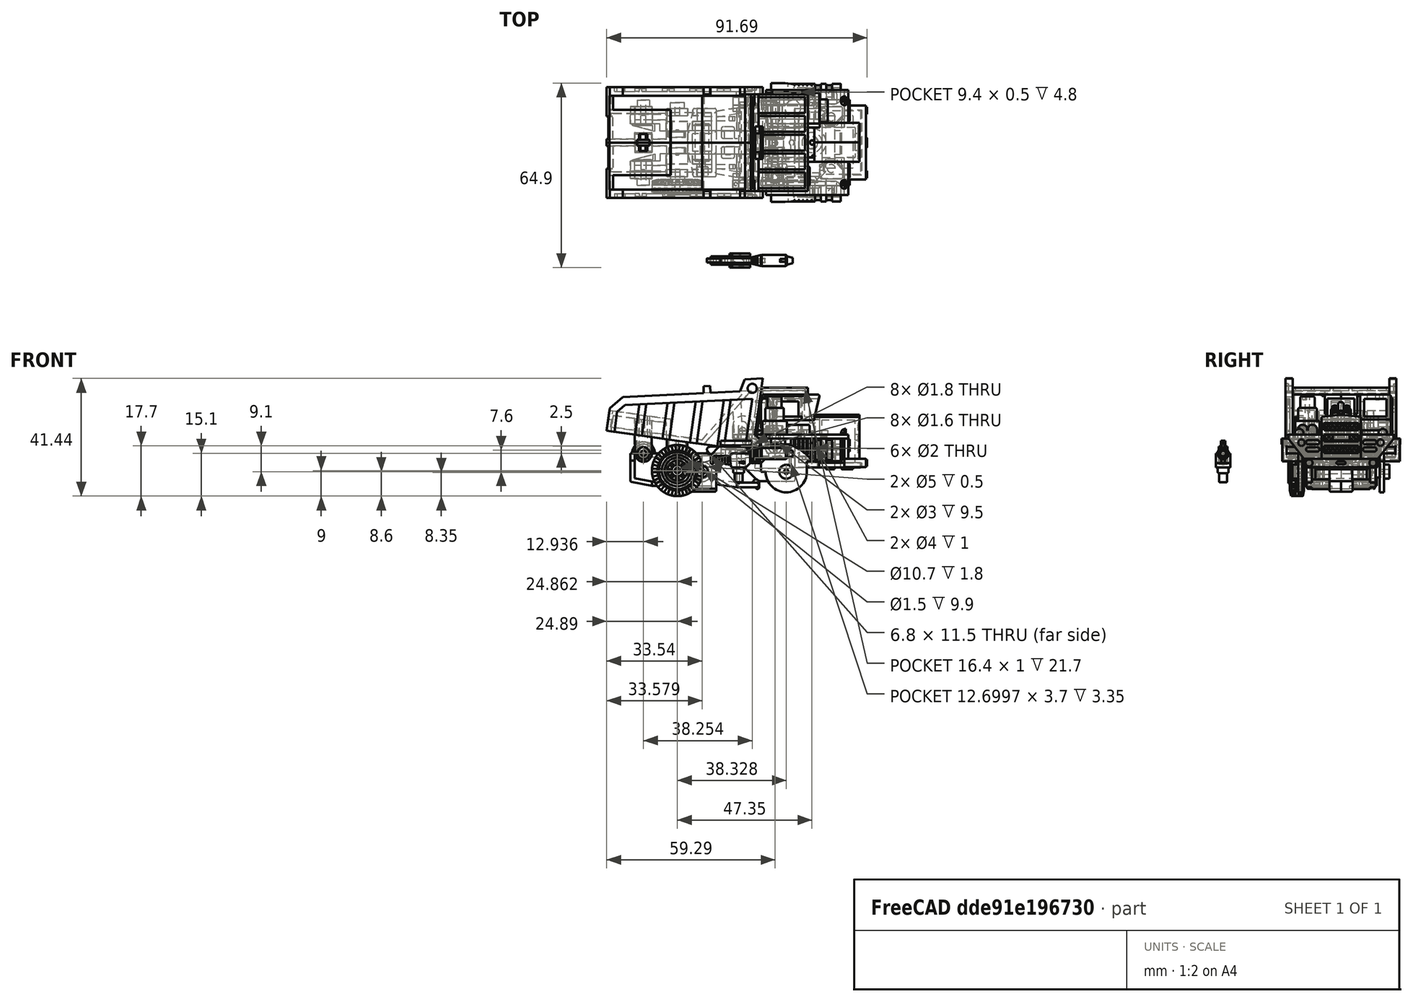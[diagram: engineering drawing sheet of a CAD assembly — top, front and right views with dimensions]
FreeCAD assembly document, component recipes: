
FREECAD ASSEMBLY — COMPONENT RECIPES ("Longhaul")

This assembly document has 21 components, labeled P0..P20 below (a component is one placed body or linked part). 19 of them carry a construction recipe — the FreeCAD feature program that regenerates the part from scratch, quoted from this document or its linked companion documents; the rest are supplied as boundary geometry only. No exploded tour is included for this assembly.
NOTE — document 3 of 4 of this assembly tour. The two overview renders and the header above are repeated from document 1; the component sections below continue where the previous document stopped.
COMPONENT P7 — recipe-attached ("Roof", modeled in this document).
Construction recipe (the document's own serialized feature program — sketch geometry with constraints, then the solid features built on it; lengths are millimeters unless a unit is written):

FEATURE [Sketcher::SketchObject] Sketch335
  ArcFitTolerance = 1e-06
  AttachmentSupport = -> [XY_Plane017]
  FullyConstrained = true
  MakeInternals = false
  MapMode = 5
  sketch-geometry (10):
    g0: LineSegment StartX=0 StartY=0 StartZ=0 EndX=16 EndY=0 EndZ=0
    g1: LineSegment StartX=16 StartY=0 StartZ=0 EndX=16 EndY=1.5 EndZ=0
    g2: LineSegment StartX=16 StartY=1.5 StartZ=0 EndX=-1.4 EndY=1.5 EndZ=0
    g3: LineSegment StartX=0 StartY=0 StartZ=0 EndX=-1.82086 EndY=-12.9561 EndZ=0
    g4: LineSegment StartX=-2.81113 StartY=-13.8169 StartZ=0 EndX=-5.72779 EndY=-13.8169 EndZ=0
    g5: ArcOfCircle CenterX=-6.8767 CenterY=-13.0169 CenterZ=0 NormalX=0 NormalY=0 NormalZ=1 AngleXU=0 Radius=1.4 StartAngle=0.608246 EndAngle=5.67494
    g6: LineSegment StartX=-5.72779 StartY=-12.2169 StartZ=0 EndX=-3.32779 EndY=-12.2169 EndZ=0
    g7: LineSegment StartX=-3.32779 StartY=-12.2169 StartZ=0 EndX=-1.4 EndY=1.5 EndZ=0
    g8: ArcOfCircle CenterX=-2.81113 CenterY=-12.8169 CenterZ=0 NormalX=0 NormalY=0 NormalZ=1 AngleXU=0 Radius=1 StartAngle=4.71239 EndAngle=6.14356
    g9: GeomPoint [constr] X=-1.94184 Y=-13.8169 Z=0
  constraints (28):
    c: Coincident(g0,g-1)
    c: PointOnObject(g0,g-1)
    c: Coincident(g1,g0)
    c: Vertical(g1)
    c: Coincident(g2,g1)
    c: Horizontal(g2)
    c: Coincident(g3,g0)
    c: Horizontal(g4)
    c: Coincident(g5,g4)
    c: Coincident(g6,g5)
    c: Horizontal(g6)
    c: Coincident(g7,g6)
    c: Coincident(g7,g2)
    c: PointOnObject(g9,g3)
    c: PointOnObject(g9,g4)
    c: Tangent(g3,g8) = 1.5708
    c: Tangent(g4,g8) = 1.5708
    c: Parallel(g3,g7)
    c: DistanceY(g4,g5) = 1.6
    c: DistanceY(g1,g1) = 1.5
    c: Distance(g4,g0) = 14.1
    c: DistanceX(g5,g4) = 0
    c: Radius(g8) = 1
    c: DistanceX(g2,g2) = 17.4
    c: Diameter(g5) = 2.8
    c: Angle(g3,g0) = 1.71042
    c: DistanceX(g6,g6) = 2.4
    c: DistanceX(g2,g0) = 1.4
FEATURE [PartDesign::Pad] Pad198
  Direction = (0,0,1)
  Length = 34
  Length2 = 10
  Profile = -> Sketch335
  ReferenceAxis = -> Sketch335 [N_Axis]
  Refine = true
  Suppressed = false
  Type = 0
FEATURE [Sketcher::SketchObject] Sketch336
  ArcFitTolerance = 1e-06
  AttachmentSupport = -> [Pad198]
  ExternalGeometry = -> [Pad198]
  FullyConstrained = true
  MakeInternals = false
  MapMode = 5
  Placement = pos=(0,0,0) rot=(1,0,0;3.14159rad)
  sketch-geometry (2):
    g0: LineSegment StartX=-5.72779 StartY=13.8169 StartZ=0 EndX=-8.02561 EndY=13.8169 EndZ=0
    g1: ArcOfCircle CenterX=-6.8767 CenterY=13.0169 CenterZ=0 NormalX=0 NormalY=0 NormalZ=1 AngleXU=0 Radius=1.39999 StartAngle=0.608239 EndAngle=2.53335
  constraints (6):
    c: Coincident(g0,g-4)
    c: PointOnObject(g0,g-4)
    c: Horizontal(g0)
    c: Coincident(g1,g0)
    c: Coincident(g1,g0)
    c: Tangent(g1,g-4)
FEATURE [PartDesign::Pocket] Pocket141
  BaseFeature = -> Pad198
  Direction = (0,0,1)
  Length = 34
  Length2 = 5
  Profile = -> Sketch336
  ReferenceAxis = -> Sketch336 [N_Axis]
  Refine = true
  Suppressed = false
  Type = 0
FEATURE [Sketcher::SketchObject] Sketch337
  ArcFitTolerance = 1e-06
  AttachmentSupport = -> [Pocket141]
  ExternalGeometry = -> [Pocket141]
  FullyConstrained = true
  MakeInternals = false
  MapMode = 5
  Placement = pos=(0,0,0) rot=(1,0,0;3.14159rad)
  sketch-geometry (7):
    g0: ArcOfCircle CenterX=-2.81113 CenterY=12.8169 CenterZ=0 NormalX=0 NormalY=0 NormalZ=1 AngleXU=0 Radius=1 StartAngle=0.139626 EndAngle=1.5708
    g1: LineSegment StartX=-1.82086 StartY=12.9561 StartZ=0 EndX=-1.125 EndY=8.00476 EndZ=0
    g2: LineSegment StartX=-1.125 StartY=8.00476 StartZ=0 EndX=-2.73581 EndY=8.00476 EndZ=0
    g3: LineSegment StartX=-2.81113 StartY=13.8169 StartZ=0 EndX=-8.02561 EndY=13.8169 EndZ=0
    g4: ArcOfCircle CenterX=-6.8767 CenterY=13.0169 CenterZ=0 NormalX=0 NormalY=0 NormalZ=1 AngleXU=0 Radius=1.4 StartAngle=2.53335 EndAngle=5.67494
    g5: LineSegment StartX=-5.72779 StartY=12.2169 StartZ=0 EndX=-3.32779 EndY=12.2169 EndZ=0
    g6: LineSegment StartX=-3.32779 StartY=12.2169 StartZ=0 EndX=-2.73581 EndY=8.00476 EndZ=0
  constraints (17):
    c: Tangent(g0,g-4) = -1.5708
    c: Coincident(g0,g-5)
    c: Radius(g0) = 1
    c: Coincident(g1,g0)
    c: PointOnObject(g1,g-5)
    c: Distance(g1) = 5
    c: Coincident(g2,g1)
    c: PointOnObject(g2,g-6)
    c: Horizontal(g2)
    c: Coincident(g3,g0)
    c: Coincident(g3,g-8)
    c: Coincident(g4,g3)
    c: Tangent(g4,g-8) = -1.5708
    c: Coincident(g5,g4)
    c: Coincident(g5,g-7)
    c: Coincident(g6,g5)
    c: Coincident(g6,g2)
FEATURE [PartDesign::Pocket] Pocket142
  BaseFeature = -> Pocket141
  Direction = (0,0,1)
  Length = 2.6
  Length2 = 5
  Profile = -> Sketch337
  ReferenceAxis = -> Sketch337 [N_Axis]
  Refine = true
  Suppressed = false
  Type = 0
FEATURE [Sketcher::SketchObject] Sketch338
  ArcFitTolerance = 1e-06
  AttachmentSupport = -> [Pocket142]
  ExternalGeometry = -> [Pocket142]
  FullyConstrained = true
  MakeInternals = false
  MapMode = 5
  Placement = pos=(0,0,34) rot=(0,0,1;0rad)
  sketch-geometry (7):
    g0: ArcOfCircle CenterX=-2.81113 CenterY=-12.8169 CenterZ=0 NormalX=0 NormalY=0 NormalZ=1 AngleXU=0 Radius=1 StartAngle=4.71239 EndAngle=6.14356
    g1: LineSegment StartX=-1.82086 StartY=-12.9561 StartZ=0 EndX=-1.125 EndY=-8.00476 EndZ=0
    g2: LineSegment StartX=-2.81113 StartY=-13.8169 StartZ=0 EndX=-8.02561 EndY=-13.8169 EndZ=0
    g3: ArcOfCircle CenterX=-6.8767 CenterY=-13.0169 CenterZ=0 NormalX=0 NormalY=0 NormalZ=1 AngleXU=0 Radius=1.4 StartAngle=0.608251 EndAngle=3.74983
    g4: LineSegment StartX=-5.72779 StartY=-12.2169 StartZ=0 EndX=-3.32779 EndY=-12.2169 EndZ=0
    g5: LineSegment StartX=-1.125 StartY=-8.00476 StartZ=0 EndX=-2.73581 EndY=-8.00476 EndZ=0
    g6: LineSegment StartX=-2.73581 StartY=-8.00476 StartZ=0 EndX=-3.32779 EndY=-12.2169 EndZ=0
  constraints (17):
    c: Coincident(g0,g-5)
    c: Tangent(g0,g-4) = -1.5708
    c: Coincident(g1,g0)
    c: PointOnObject(g1,g-3)
    c: Distance(g1) = 5
    c: Coincident(g2,g0)
    c: Coincident(g2,g-6)
    c: Coincident(g3,g2)
    c: Coincident(g3,g-7)
    c: Tangent(g3,g-6)
    c: Coincident(g4,g3)
    c: Coincident(g4,g-8)
    c: Coincident(g5,g1)
    c: PointOnObject(g5,g-8)
    c: Horizontal(g5)
    c: Coincident(g6,g5)
    c: Coincident(g6,g4)
FEATURE [PartDesign::Pocket] Pocket143
  BaseFeature = -> Pocket142
  Direction = (0,0,-1)
  Length = 2.6
  Length2 = 5
  Profile = -> Sketch338
  ReferenceAxis = -> Sketch338 [N_Axis]
  Refine = true
  Suppressed = false
  Type = 0
FEATURE [Sketcher::SketchObject] Sketch339
  ArcFitTolerance = 1e-06
  AttachmentSupport = -> [Pocket143]
  ExternalGeometry = -> [Pocket143]
  FullyConstrained = true
  MakeInternals = false
  MapMode = 5
  Placement = pos=(0,0,31.4) rot=(0,0,1;0rad)
  sketch-geometry (7):
    g0: ArcOfCircle CenterX=-6.8767 CenterY=-13.0169 CenterZ=0 NormalX=0 NormalY=0 NormalZ=1 AngleXU=0 Radius=1.4 StartAngle=5.67495 EndAngle=6.89144
    g1: LineSegment StartX=-5.72778 StartY=-13.8169 StartZ=0 EndX=-2.81113 EndY=-13.8169 EndZ=0
    g2: LineSegment StartX=-5.72779 StartY=-12.2169 StartZ=0 EndX=-3.32779 EndY=-12.2169 EndZ=0
    g3: LineSegment StartX=-3.32779 StartY=-12.2169 StartZ=0 EndX=-2.73581 EndY=-8.00476 EndZ=0
    g4: LineSegment StartX=-2.73581 StartY=-8.00476 StartZ=0 EndX=-1.125 EndY=-8.00476 EndZ=0
    g5: ArcOfCircle CenterX=-2.81113 CenterY=-12.8169 CenterZ=0 NormalX=0 NormalY=0 NormalZ=1 AngleXU=0 Radius=1 StartAngle=4.71239 EndAngle=6.14356
    g6: LineSegment StartX=-1.125 StartY=-8.00476 StartZ=0 EndX=-1.82086 EndY=-12.9561 EndZ=0
  constraints (15):
    c: PointOnObject(g0,g-8)
    c: Coincident(g0,g-7)
    c: Coincident(g1,g0)
    c: Coincident(g1,g-9)
    c: Coincident(g0,g-7)
    c: Coincident(g2,g0)
    c: Coincident(g2,g-6)
    c: Coincident(g3,g2)
    c: Coincident(g3,g-5)
    c: Coincident(g4,g3)
    c: Coincident(g4,g-4)
    c: Coincident(g5,g1)
    c: Tangent(g5,g-9) = -1.5708
    c: Coincident(g6,g4)
    c: Coincident(g6,g5)
FEATURE [PartDesign::Pocket] Pocket144
  BaseFeature = -> Pocket143
  Direction = (0,0,-1)
  Length = 1.3
  Length2 = 5
  Profile = -> Sketch339
  ReferenceAxis = -> Sketch339 [N_Axis]
  Refine = true
  Suppressed = false
  Type = 0
FEATURE [Sketcher::SketchObject] Sketch340
  ArcFitTolerance = 1e-06
  AttachmentSupport = -> [Pocket144]
  ExternalGeometry = -> [Pocket144]
  FullyConstrained = true
  MakeInternals = false
  MapMode = 5
  Placement = pos=(0,0,2.6) rot=(1,0,0;3.14159rad)
  sketch-geometry (7):
    g0: ArcOfCircle CenterX=-6.8767 CenterY=13.0169 CenterZ=0 NormalX=0 NormalY=0 NormalZ=1 AngleXU=0 Radius=1.4 StartAngle=5.67494 EndAngle=6.89143
    g1: ArcOfCircle CenterX=-2.81113 CenterY=12.8169 CenterZ=0 NormalX=0 NormalY=0 NormalZ=1 AngleXU=0 Radius=1 StartAngle=0.139626 EndAngle=1.5708
    g2: LineSegment StartX=-5.72779 StartY=13.8169 StartZ=0 EndX=-2.81113 EndY=13.8169 EndZ=0
    g3: LineSegment StartX=-5.72779 StartY=12.2169 StartZ=0 EndX=-3.32779 EndY=12.2169 EndZ=0
    g4: LineSegment StartX=-1.82086 StartY=12.9561 StartZ=0 EndX=-1.125 EndY=8.00476 EndZ=0
    g5: LineSegment StartX=-3.32779 StartY=12.2169 StartZ=0 EndX=-2.73581 EndY=8.00476 EndZ=0
    g6: LineSegment StartX=-2.73581 StartY=8.00476 StartZ=0 EndX=-1.125 EndY=8.00476 EndZ=0
  constraints (15):
    c: Coincident(g0,g-7)
    c: PointOnObject(g0,g-5)
    c: Coincident(g0,g-7)
    c: Coincident(g1,g-5)
    c: Tangent(g1,g-4) = -1.5708
    c: Coincident(g2,g0)
    c: Coincident(g2,g1)
    c: Coincident(g3,g0)
    c: Coincident(g3,g-6)
    c: Coincident(g4,g1)
    c: Coincident(g4,g-8)
    c: Coincident(g5,g3)
    c: Coincident(g5,g-8)
    c: Coincident(g6,g5)
    c: Coincident(g6,g4)
FEATURE [PartDesign::Pocket] Pocket145
  BaseFeature = -> Pocket144
  Direction = (0,0,1)
  Length = 1.3
  Length2 = 5
  Profile = -> Sketch340
  ReferenceAxis = -> Sketch340 [N_Axis]
  Refine = true
  Suppressed = false
  Type = 0
FEATURE [Sketcher::SketchObject] Sketch341
  ArcFitTolerance = 1e-06
  AttachmentSupport = -> [Pocket145]
  ExternalGeometry = -> [Pocket145]
  FullyConstrained = true
  MakeInternals = false
  MapMode = 5
  Placement = pos=(-1.57961,0.222,0) rot=(-0.523661,0.602403,0.602403;4.10639rad)
  sketch-geometry (4):
    g0: LineSegment StartX=12.5612 StartY=13.75 StartZ=0 EndX=12.5612 EndY=20.25 EndZ=0
    g1: LineSegment StartX=12.5612 StartY=20.25 StartZ=0 EndX=11.5612 EndY=20.25 EndZ=0
    g2: LineSegment StartX=11.5612 StartY=20.25 StartZ=0 EndX=11.5612 EndY=13.75 EndZ=0
    g3: LineSegment StartX=11.5612 StartY=13.75 StartZ=0 EndX=12.5612 EndY=13.75 EndZ=0
  constraints (14):
    c: Coincident(g0,g1)
    c: Coincident(g1,g2)
    c: Coincident(g2,g3)
    c: Coincident(g3,g0)
    c: Vertical(g0)
    c: Vertical(g2)
    c: Horizontal(g1)
    c: Horizontal(g3)
    c: PointOnObject(g0,g-4)
    c: DistanceY(g2,g2) = 6.5
    c: DistanceX(g3,g3) = 1
    c: DistanceY(g-4,g-5) = 26.2
    c: DistanceY(g-3,g-3) = 0
    c: DistanceY(g-4,g0) = 9.85
FEATURE [PartDesign::Pad] Pad199
  BaseFeature = -> Pocket145
  Direction = (-0.990268,0.139173,0)
  Length = 0.5
  Length2 = 10
  Profile = -> Sketch341
  ReferenceAxis = -> Sketch341 [N_Axis]
  Refine = true
  Suppressed = false
  Type = 0
FEATURE [Sketcher::SketchObject] Sketch342
  ArcFitTolerance = 1e-06
  AttachmentSupport = -> [Pad199]
  ExternalGeometry = -> [Pad199]
  FullyConstrained = false
  MakeInternals = false
  MapMode = 5
  Placement = pos=(-2.07475,0.291586,0) rot=(-0.523661,0.602403,0.602403;4.10639rad)
  sketch-geometry (4):
    g0: LineSegment StartX=12.5612 StartY=20.25 StartZ=0 EndX=12.5612 EndY=13.75 EndZ=0
    g1: LineSegment StartX=12.5612 StartY=13.75 StartZ=0 EndX=13.9707 EndY=13.75 EndZ=0
    g2: LineSegment StartX=13.9707 StartY=13.75 StartZ=0 EndX=13.9707 EndY=20.25 EndZ=0
    g3: LineSegment StartX=13.9707 StartY=20.25 StartZ=0 EndX=12.5612 EndY=20.25 EndZ=0
  constraints (9):
    c: Coincident(g0,g1)
    c: Coincident(g1,g2)
    c: Coincident(g2,g3)
    c: Coincident(g3,g0)
    c: Vertical(g2)
    c: Horizontal(g1)
    c: Horizontal(g3)
    c: Coincident(g0,g-5)
    c: Coincident(g0,g-5)
FEATURE [PartDesign::Pad] Pad200
  BaseFeature = -> Pad199
  Direction = (-0.990268,0.139173,2e-16)
  Length = 0.5
  Length2 = 10
  Profile = -> Sketch342
  ReferenceAxis = -> Sketch342 [N_Axis]
  Refine = true
  Reversed = true
  Suppressed = false
  Type = 0
FEATURE [Sketcher::SketchObject] Sketch343
  ArcFitTolerance = 1e-06
  AttachmentSupport = -> [Pad200]
  ExternalGeometry = -> [Pad200]
  FullyConstrained = true
  MakeInternals = false
  MapMode = 5
  Placement = pos=(-1.57961,0.222,0) rot=(-0.523661,0.602403,0.602403;4.10639rad)
  sketch-geometry (4):
    g0: LineSegment StartX=-1.29056 StartY=22.7 StartZ=0 EndX=-1.29056 EndY=11.3 EndZ=0
    g1: LineSegment StartX=-1.29056 StartY=11.3 StartZ=0 EndX=5.90944 EndY=11.3 EndZ=0
    g2: LineSegment StartX=5.90944 StartY=11.3 StartZ=0 EndX=5.90944 EndY=22.7 EndZ=0
    g3: LineSegment StartX=5.90944 StartY=22.7 StartZ=0 EndX=-1.29056 EndY=22.7 EndZ=0
  constraints (13):
    c: Coincident(g0,g1)
    c: Coincident(g1,g2)
    c: Coincident(g2,g3)
    c: Coincident(g3,g0)
    c: Vertical(g0)
    c: Vertical(g2)
    c: Horizontal(g1)
    c: Horizontal(g3)
    c: PointOnObject(g0,g-3)
    c: DistanceY(g2,g2) = 11.4
    c: DistanceX(g3,g3) = 7.2
    c: DistanceY(g-3,g-3) = 34
    c: DistanceY(g-3,g0) = 11.3
FEATURE [PartDesign::Pocket] Pocket146
  BaseFeature = -> Pad200
  Direction = (0.990268,-0.139173,0)
  Length = 1.6
  Length2 = 5
  Profile = -> Sketch343
  ReferenceAxis = -> Sketch343 [N_Axis]
  Refine = true
  Suppressed = false
  Type = 0
FEATURE [Sketcher::SketchObject] Sketch344
  ArcFitTolerance = 1e-06
  AttachmentSupport = -> [Pocket146]
  ExternalGeometry = -> [Pocket146]
  FullyConstrained = true
  MakeInternals = false
  MapMode = 5
  Placement = pos=(0,1.5,0) rot=(0,0.707107,0.707107;3.14159rad)
  sketch-geometry (24):
    g0: LineSegment StartX=1.4 StartY=0 StartZ=0 EndX=1.4 EndY=1 EndZ=0
    g1: LineSegment StartX=1.4 StartY=1 StartZ=0 EndX=-15 EndY=1 EndZ=0
    g2: LineSegment StartX=-15 StartY=1 StartZ=0 EndX=-15 EndY=6.6 EndZ=0
    g3: LineSegment StartX=-15 StartY=6.6 StartZ=0 EndX=1.4 EndY=6.6 EndZ=0
    g4: LineSegment StartX=1.4 StartY=6.6 StartZ=0 EndX=1.4 EndY=7.6 EndZ=0
    g5: LineSegment StartX=1.4 StartY=7.6 StartZ=0 EndX=-15 EndY=7.6 EndZ=0
    g6: LineSegment StartX=-15 StartY=7.6 StartZ=0 EndX=-15 EndY=13.2 EndZ=0
    g7: LineSegment StartX=-15 StartY=13.2 StartZ=0 EndX=1.4 EndY=13.2 EndZ=0
    g8: LineSegment StartX=1.4 StartY=13.2 StartZ=0 EndX=1.4 EndY=14.2 EndZ=0
    g9: LineSegment StartX=1.4 StartY=14.2 StartZ=0 EndX=-15 EndY=14.2 EndZ=0
    g10: LineSegment StartX=-15 StartY=14.2 StartZ=0 EndX=-15 EndY=19.8 EndZ=0
    g11: LineSegment StartX=-15 StartY=19.8 StartZ=0 EndX=1.4 EndY=19.8 EndZ=0
    g12: LineSegment StartX=1.4 StartY=19.8 StartZ=0 EndX=1.4 EndY=20.8 EndZ=0
    g13: LineSegment StartX=1.4 StartY=20.8 StartZ=0 EndX=-15 EndY=20.8 EndZ=0
    g14: LineSegment StartX=-15 StartY=33 StartZ=0 EndX=1.4 EndY=33 EndZ=0
    g15: LineSegment StartX=1.4 StartY=33 StartZ=0 EndX=1.4 EndY=34 EndZ=0
    g16: LineSegment StartX=1.4 StartY=34 StartZ=0 EndX=-16 EndY=34 EndZ=0
    g17: LineSegment StartX=-16 StartY=34 StartZ=0 EndX=-16 EndY=0 EndZ=0
    g18: LineSegment StartX=-16 StartY=0 StartZ=0 EndX=1.4 EndY=0 EndZ=0
    g19: LineSegment StartX=-15 StartY=20.8 StartZ=0 EndX=-15 EndY=26.4 EndZ=0
    g20: LineSegment StartX=-15 StartY=26.4 StartZ=0 EndX=1.4 EndY=26.4 EndZ=0
    g21: LineSegment StartX=1.4 StartY=26.4 StartZ=0 EndX=1.4 EndY=27.4 EndZ=0
    g22: LineSegment StartX=1.4 StartY=27.4 StartZ=0 EndX=-15 EndY=27.4 EndZ=0
    g23: LineSegment StartX=-15 StartY=27.4 StartZ=0 EndX=-15 EndY=33 EndZ=0
  constraints (68):
    c: Coincident(g0,g-5)
    c: Vertical(g0)
    c: Coincident(g1,g0)
    c: Horizontal(g1)
    c: Coincident(g2,g1)
    c: Vertical(g2)
    c: Coincident(g3,g2)
    c: PointOnObject(g3,g-6)
    c: Horizontal(g3)
    c: Coincident(g4,g3)
    c: PointOnObject(g4,g-6)
    c: Coincident(g5,g4)
    c: Horizontal(g5)
    c: Coincident(g6,g5)
    c: Vertical(g6)
    c: Coincident(g7,g6)
    c: PointOnObject(g7,g-7)
    c: Horizontal(g7)
    c: Coincident(g8,g7)
    c: PointOnObject(g8,g-7)
    c: Coincident(g9,g8)
    c: Horizontal(g9)
    c: Coincident(g10,g9)
    c: Vertical(g10)
    c: Coincident(g11,g10)
    c: PointOnObject(g11,g-8)
    c: Horizontal(g11)
    c: Coincident(g12,g11)
    c: PointOnObject(g12,g-8)
    c: Coincident(g13,g12)
    c: Horizontal(g13)
    c: PointOnObject(g14,g-8)
    c: Horizontal(g14)
    c: Coincident(g15,g14)
    c: Coincident(g15,g-8)
    c: Coincident(g16,g15)
    c: Coincident(g16,g-4)
    c: Coincident(g17,g16)
    c: Coincident(g17,g-5)
    c: Coincident(g18,g17)
    c: Coincident(g18,g0)
    c: DistanceY(g0,g0) = 1
    c: DistanceY(g4,g4) = 1
    c: DistanceY(g8,g8) = 1
    c: DistanceY(g12,g12) = 1
    c: DistanceY(g15,g15) = 1
    c: DistanceX(g16,g14) = 1
    c: DistanceX(g13,g10) = 0
    c: DistanceX(g9,g6) = 0
    c: DistanceX(g5,g2) = 0
    c: DistanceY(g2,g2) = 5.6
    c: DistanceY(g6,g6) = 5.6
    c: DistanceY(g10,g10) = 5.6
    c: Coincident(g19,g13)
    c: Vertical(g19)
    c: Coincident(g20,g19)
    c: PointOnObject(g20,g-8)
    c: Horizontal(g20)
    c: Coincident(g21,g20)
    c: PointOnObject(g21,g-8)
    c: Coincident(g22,g21)
    c: Horizontal(g22)
    c: Coincident(g23,g22)
    c: Coincident(g23,g14)
    c: Vertical(g23)
    c: DistanceY(g21,g21) = 1
    c: DistanceY(g19,g19) = 5.6
    c: DistanceX(g22,g19) = 0
FEATURE [PartDesign::Pad] Pad201
  BaseFeature = -> Pocket146
  Direction = (0,1,-2e-16)
  Length = 1
  Length2 = 10
  Profile = -> Sketch344
  ReferenceAxis = -> Sketch344 [N_Axis]
  Refine = true
  Suppressed = false
  Type = 0
FEATURE [Sketcher::SketchObject] Sketch345
  ArcFitTolerance = 1e-06
  AttachmentSupport = -> [Pad201]
  ExternalGeometry = -> [Pad201]
  FullyConstrained = true
  MakeInternals = false
  MapMode = 5
  Placement = pos=(0,0,0) rot=(1,0,0;1.5708rad)
  sketch-geometry (8):
    g0: LineSegment StartX=2 StartY=22.7 StartZ=0 EndX=14 EndY=22.7 EndZ=0
    g1: LineSegment StartX=14 StartY=23.7 StartZ=0 EndX=2 EndY=23.7 EndZ=0
    g2: LineSegment StartX=2 StartY=10.3 StartZ=0 EndX=14 EndY=10.3 EndZ=0
    g3: LineSegment StartX=14 StartY=11.3 StartZ=0 EndX=2 EndY=11.3 EndZ=0
    g4: ArcOfCircle CenterX=14 CenterY=23.2 CenterZ=0 NormalX=0 NormalY=0 NormalZ=1 AngleXU=0 Radius=0.5 StartAngle=4.71239 EndAngle=7.85398
    g5: ArcOfCircle CenterX=2 CenterY=23.2 CenterZ=0 NormalX=0 NormalY=0 NormalZ=1 AngleXU=0 Radius=0.5 StartAngle=1.5708 EndAngle=4.71239
    g6: ArcOfCircle CenterX=2 CenterY=10.8 CenterZ=0 NormalX=0 NormalY=0 NormalZ=1 AngleXU=0 Radius=0.5 StartAngle=1.5708 EndAngle=4.71239
    g7: ArcOfCircle CenterX=14 CenterY=10.8 CenterZ=0 NormalX=0 NormalY=0 NormalZ=1 AngleXU=0 Radius=0.5 StartAngle=4.71239 EndAngle=7.85398
  constraints (29):
    c: Horizontal(g0)
    c: Horizontal(g1)
    c: Horizontal(g2)
    c: Horizontal(g3)
    c: Coincident(g4,g1)
    c: Coincident(g4,g0)
    c: Coincident(g5,g1)
    c: Coincident(g5,g0)
    c: Coincident(g6,g3)
    c: Coincident(g6,g2)
    c: Coincident(g7,g3)
    c: Coincident(g7,g2)
    c: Diameter(g6) = 1
    c: Diameter(g5) = 1
    c: DistanceY(g4,g-3) = 10.8
    c: DistanceY(g-4,g7) = 10.8
    c: DistanceX(g1,g1) = 12
    c: DistanceX(g-3,g-3) = 16
    c: DistanceX(g-3,g5) = 2
    c: DistanceX(g3,g3) = 12
    c: DistanceX(g2,g-4) = 2
    c: Diameter(g7) = 1
    c: Diameter(g4) = 1
    c: DistanceX(g4,g1) = 0
    c: DistanceX(g4,g0) = 0
    c: DistanceX(g1,g5) = 0
    c: DistanceX(g3,g6) = 0
    c: DistanceX(g2,g6) = 0
    c: DistanceX(g7,g3) = 0
FEATURE [PartDesign::Pad] Pad202
  BaseFeature = -> Pad201
  Direction = (0,-1,2e-16)
  Length = 0.5
  Length2 = 10
  Profile = -> Sketch345
  ReferenceAxis = -> Sketch345 [N_Axis]
  Refine = true
  Suppressed = false
  Type = 0
FEATURE [Sketcher::SketchObject] Sketch346
  ArcFitTolerance = 1e-06
  AttachmentSupport = -> [Pad202]
  ExternalGeometry = -> [Pad202]
  FullyConstrained = true
  MakeInternals = false
  MapMode = 5
  Placement = pos=(0,0,0) rot=(1,0,0;1.5708rad)
  sketch-geometry (8):
    g0: LineSegment StartX=1.7 StartY=30.5 StartZ=0 EndX=-0.6 EndY=30.5 EndZ=0
    g1: LineSegment StartX=-0.6 StartY=30.5 StartZ=0 EndX=-0.6 EndY=29.2 EndZ=0
    g2: LineSegment StartX=-0.6 StartY=29.2 StartZ=0 EndX=1.7 EndY=29.2 EndZ=0
    g3: LineSegment StartX=1.7 StartY=29.2 StartZ=0 EndX=1.7 EndY=30.5 EndZ=0
    g4: LineSegment StartX=1.7 StartY=4.8 StartZ=0 EndX=-0.6 EndY=4.8 EndZ=0
    g5: LineSegment StartX=-0.6 StartY=4.8 StartZ=0 EndX=-0.6 EndY=3.5 EndZ=0
    g6: LineSegment StartX=-0.6 StartY=3.5 StartZ=0 EndX=1.7 EndY=3.5 EndZ=0
    g7: LineSegment StartX=1.7 StartY=3.5 StartZ=0 EndX=1.7 EndY=4.8 EndZ=0
  constraints (24):
    c: Coincident(g0,g1)
    c: Coincident(g1,g2)
    c: Coincident(g2,g3)
    c: Coincident(g3,g0)
    c: Horizontal(g0)
    c: Horizontal(g2)
    c: Vertical(g1)
    c: Vertical(g3)
    c: Coincident(g4,g5)
    c: Coincident(g5,g6)
    c: Coincident(g6,g7)
    c: Coincident(g7,g4)
    c: Horizontal(g4)
    c: Horizontal(g6)
    c: Vertical(g5)
    c: Vertical(g7)
    c: DistanceX(g6,g-3) = 14.3
    c: DistanceX(g0,g-3) = 14.3
    c: DistanceY(g3,g3) = 1.3
    c: DistanceY(g7,g7) = 1.3
    c: DistanceY(g-1,g6) = 3.5
    c: DistanceY(g0,g-4) = 3.5
    c: DistanceX(g0,g0) = 2.3
    c: DistanceX(g4,g4) = 2.3
FEATURE [PartDesign::Pad] Pad203
  BaseFeature = -> Pad202
  Direction = (0,-1,2e-16)
  Length = 1.8
  Length2 = 10
  Profile = -> Sketch346
  ReferenceAxis = -> Sketch346 [N_Axis]
  Refine = true
  Suppressed = false
  Type = 0
FEATURE [Sketcher::SketchObject] Sketch347
  ArcFitTolerance = 1e-06
  AttachmentSupport = -> [Pad203]
  ExternalGeometry = -> [Pad203]
  FullyConstrained = false
  MakeInternals = false
  MapMode = 5
  Placement = pos=(0,6.7e-15,30.5) rot=(0,0,1;0rad)
  sketch-geometry (4):
    g0: LineSegment StartX=1.7 StartY=0 StartZ=0 EndX=1.7 EndY=-1.8 EndZ=0
    g1: LineSegment StartX=1.7 StartY=-1.8 StartZ=0 EndX=-0.252974 EndY=-1.8 EndZ=0
    g2: LineSegment StartX=1.7 StartY=0 StartZ=0 EndX=1.45 EndY=0 EndZ=0
    g3: LineSegment StartX=-0.252974 StartY=-1.8 StartZ=0 EndX=1.45 EndY=0 EndZ=0
  constraints (8):
    c: Coincident(g0,g-6)
    c: Coincident(g1,g0)
    c: Coincident(g2,g0)
    c: PointOnObject(g2,g-3)
    c: Horizontal(g2)
    c: DistanceX(g2,g2) = 0.25
    c: Coincident(g3,g1)
    c: Coincident(g3,g2)
FEATURE [PartDesign::Pocket] Pocket147
  BaseFeature = -> Pad203
  Direction = (0,0,-1)
  Length = 1.3
  Length2 = 5
  Profile = -> Sketch347
  ReferenceAxis = -> Sketch347 [N_Axis]
  Refine = true
  Suppressed = false
  Type = 0
FEATURE [Sketcher::SketchObject] Sketch348
  ArcFitTolerance = 1e-06
  AttachmentOffset = pos=(0,3.8,10.1) rot=(-1,0,0;0.785398rad)
  AttachmentSupport = -> [Pocket147]
  ExternalGeometry = -> [Pocket147]
  FullyConstrained = false
  MakeInternals = false
  MapMode = 5
  Placement = pos=(0,-3.8,-6.6) rot=(1,0,0;2.35619rad)
  sketch-geometry (4):
    g0: LineSegment StartX=-8.90083 StartY=11.4236 StartZ=0 EndX=-4.94936 EndY=11.4236 EndZ=0
    g1: LineSegment StartX=-4.94936 StartY=11.4236 StartZ=0 EndX=-4.94936 EndY=12.9245 EndZ=0
    g2: LineSegment StartX=-4.94936 StartY=12.9245 StartZ=0 EndX=-8.90083 EndY=12.9245 EndZ=0
    g3: LineSegment StartX=-8.90083 StartY=12.9245 StartZ=0 EndX=-8.90083 EndY=11.4236 EndZ=0
  constraints (8):
    c: Coincident(g0,g1)
    c: Coincident(g1,g2)
    c: Coincident(g2,g3)
    c: Coincident(g3,g0)
    c: Horizontal(g0)
    c: Horizontal(g2)
    c: Vertical(g1)
    c: Vertical(g3)
FEATURE [PartDesign::Pocket] Pocket148
  BaseFeature = -> Pocket147
  Direction = (0,0.707107,0.707107)
  Length = 2.3
  Length2 = 5
  Profile = -> Sketch348
  ReferenceAxis = -> Sketch348 [N_Axis]
  Refine = true
  Suppressed = false
  Type = 0
FEATURE [Sketcher::SketchObject] Sketch349
  ArcFitTolerance = 1e-06
  AttachmentOffset = pos=(0,-6.5,-6.5) rot=(1,0,0;-0.785398rad)
  AttachmentSupport = -> [Pocket148]
  ExternalGeometry = -> [Pocket148]
  FullyConstrained = true
  MakeInternals = false
  MapMode = 5
  Placement = pos=(0,-6.5,24.9) rot=(1,0,0;5.49779rad)
  sketch-geometry (4):
    g0: LineSegment StartX=-5.4767 StartY=-9.20436 StartZ=0 EndX=-5.4767 EndY=-7.20436 EndZ=0
    g1: LineSegment StartX=-5.4767 StartY=-7.20436 StartZ=0 EndX=-8.2767 EndY=-7.20436 EndZ=0
    g2: LineSegment StartX=-8.2767 StartY=-9.20436 StartZ=0 EndX=-5.4767 EndY=-9.20436 EndZ=0
    g3: LineSegment StartX=-8.2767 StartY=-7.20436 StartZ=0 EndX=-8.2767 EndY=-9.20436 EndZ=0
  constraints (12):
    c: Coincident(g0,g1)
    c: Coincident(g2,g0)
    c: Vertical(g0)
    c: Horizontal(g1)
    c: Horizontal(g2)
    c: PointOnObject(g-4,g2)
    c: Coincident(g3,g1)
    c: Coincident(g3,g2)
    c: Vertical(g3)
    c: DistanceX(g2,g-4) = 1.4
    c: DistanceX(g-4,g0) = 1.4
    c: DistanceY(g3,g3) = 2
FEATURE [PartDesign::Pocket] Pocket149
  BaseFeature = -> Pocket148
  Direction = (0,-0.707107,-0.707107)
  Length = 5
  Length2 = 5
  Profile = -> Sketch349
  ReferenceAxis = -> Sketch349 [N_Axis]
  Refine = true
  Reversed = true
  Suppressed = false
  Type = 0
FEATURE [Sketcher::SketchObject] Sketch366
  ArcFitTolerance = 1e-06
  AttachmentSupport = -> [Pocket149]
  ExternalGeometry = -> [Pocket149]
  FullyConstrained = true
  MakeInternals = false
  MapMode = 5
  Placement = pos=(0,1.5,0) rot=(0,0.707107,0.707107;3.14159rad)
  sketch-geometry (4):
    g0: LineSegment StartX=1.4 StartY=22.7 StartZ=0 EndX=-0.2 EndY=22.7 EndZ=0
    g1: LineSegment StartX=-0.2 StartY=22.7 StartZ=0 EndX=-0.2 EndY=11.3 EndZ=0
    g2: LineSegment StartX=-0.2 StartY=11.3 StartZ=0 EndX=1.4 EndY=11.3 EndZ=0
    g3: LineSegment StartX=1.4 StartY=11.3 StartZ=0 EndX=1.4 EndY=22.7 EndZ=0
  constraints (10):
    c: Coincident(g0,g1)
    c: Coincident(g1,g2)
    c: Coincident(g2,g3)
    c: Coincident(g3,g0)
    c: Horizontal(g0)
    c: Horizontal(g2)
    c: Vertical(g1)
    c: Coincident(g2,g-4)
    c: Coincident(g0,g-3)
    c: DistanceX(g0,g0) = 1.6
FEATURE [PartDesign::Pocket] Pocket156
  BaseFeature = -> Pocket149
  Direction = (0,-1,2e-16)
  Length = 5
  Length2 = 5
  Profile = -> Sketch366
  ReferenceAxis = -> Sketch366 [N_Axis]
  Refine = true
  Suppressed = false
  Type = 0
FEATURE [PartDesign::Pocket] Pocket157
  BaseFeature = -> Pocket156
  Direction = (0,-1,2e-16)
  Length = 5
  Length2 = 5
  Profile = -> Sketch366
  ReferenceAxis = -> Sketch366 [N_Axis]
  Refine = true
  Reversed = true
  Suppressed = false
  Type = 0
FEATURE [Sketcher::SketchObject] Sketch367
  ArcFitTolerance = 1e-06
  AttachmentSupport = -> [Pocket157]
  ExternalGeometry = -> [Pocket157]
  FullyConstrained = true
  MakeInternals = false
  MapMode = 5
  Placement = pos=(-0.822435,-5.85193,0) rot=(0.049385,0.706244,0.706244;3.0429rad)
  sketch-geometry (4):
    g0: LineSegment StartX=1.59513 StartY=11.3 StartZ=0 EndX=1.59513 EndY=22.7 EndZ=0
    g1: LineSegment StartX=1.59513 StartY=22.7 StartZ=0 EndX=0 EndY=22.7 EndZ=0
    g2: LineSegment StartX=0 StartY=22.7 StartZ=0 EndX=0 EndY=11.3 EndZ=0
    g3: LineSegment StartX=0 StartY=11.3 StartZ=0 EndX=1.59513 EndY=11.3 EndZ=0
  constraints (10):
    c: Coincident(g0,g1)
    c: Coincident(g1,g2)
    c: Coincident(g2,g3)
    c: Coincident(g3,g0)
    c: Vertical(g0)
    c: Vertical(g2)
    c: Horizontal(g1)
    c: Horizontal(g3)
    c: Coincident(g0,g-4)
    c: Coincident(g1,g-3)
FEATURE [PartDesign::Pocket] Pocket158
  BaseFeature = -> Pocket157
  Direction = (-0.139173,-0.990268,2e-16)
  Length = 1
  Length2 = 5
  Profile = -> Sketch367
  ReferenceAxis = -> Sketch367 [N_Axis]
  Refine = true
  Suppressed = false
  Type = 0
FEATURE [Sketcher::SketchObject] Sketch369
  ArcFitTolerance = 1e-06
  AttachmentOffset = pos=(0,0,-17.5) rot=(0,0,1;0rad)
  AttachmentSupport = -> [Pocket158]
  FullyConstrained = true
  MakeInternals = false
  MapMode = 5
  Placement = pos=(-1.5,-5.6e-15,0) rot=(0.57735,0.57735,0.57735;2.0944rad)
  sketch-geometry (4):
    g0: LineSegment StartX=-13.8169 StartY=19.5 StartZ=0 EndX=-13.8169 EndY=14.5 EndZ=0
    g1: LineSegment StartX=-13.8169 StartY=14.5 StartZ=0 EndX=-12.3169 EndY=14.5 EndZ=0
    g2: LineSegment StartX=-12.3169 StartY=14.5 StartZ=0 EndX=-12.3169 EndY=19.5 EndZ=0
    g3: LineSegment StartX=-12.3169 StartY=19.5 StartZ=0 EndX=-13.8169 EndY=19.5 EndZ=0
  constraints (13):
    c: Coincident(g0,g1)
    c: Coincident(g1,g2)
    c: Coincident(g2,g3)
    c: Coincident(g3,g0)
    c: Vertical(g0)
    c: Vertical(g2)
    c: Horizontal(g1)
    c: Horizontal(g3)
    c: PointOnObject(g0,g-3)
    c: DistanceY(g2,g2) = 5
    c: DistanceX(g1,g1) = 1.5
    c: DistanceY(g-3,g-3) = 26.2
    c: DistanceY(g-3,g0) = 10.6
FEATURE [PartDesign::Pocket] Pocket159
  BaseFeature = -> Pocket158
  Direction = (-1,0,0)
  Length = 1.5
  Length2 = 5
  Profile = -> Sketch369
  ReferenceAxis = -> Sketch369 [N_Axis]
  Refine = true
  Suppressed = false
  Type = 0
FEATURE [Sketcher::SketchObject] Sketch371
  ArcFitTolerance = 1e-06
  AttachmentSupport = -> [Pocket159]
  ExternalGeometry = -> [Pocket159]
  FullyConstrained = true
  MakeInternals = false
  MapMode = 5
  Placement = pos=(0,0,2.6) rot=(1,0,0;3.14159rad)
  sketch-geometry (6):
    g0: LineSegment StartX=-5.72779 StartY=13.8169 StartZ=0 EndX=-8.02561 EndY=13.8169 EndZ=0
    g1: ArcOfCircle CenterX=-6.8767 CenterY=13.0169 CenterZ=0 NormalX=0 NormalY=0 NormalZ=1 AngleXU=0 Radius=1.4 StartAngle=2.53335 EndAngle=3.24099
    g2: ArcOfCircle CenterX=-6.8767 CenterY=13.0169 CenterZ=0 NormalX=0 NormalY=0 NormalZ=1 AngleXU=0 Radius=1.4 StartAngle=6.18379 EndAngle=6.89143
    g3: LineSegment StartX=-8.26979 StartY=12.878 StartZ=0 EndX=-8.26979 EndY=12.178 EndZ=0
    g4: LineSegment StartX=-5.48361 StartY=12.878 StartZ=0 EndX=-5.48361 EndY=12.178 EndZ=0
    g5: LineSegment StartX=-8.26979 StartY=12.178 StartZ=0 EndX=-5.48361 EndY=12.178 EndZ=0
  constraints (14):
    c: Coincident(g0,g-4)
    c: Coincident(g0,g-5)
    c: Coincident(g1,g0)
    c: Tangent(g1,g-5) = -1.5708
    c: Coincident(g2,g0)
    c: Tangent(g2,g-4) = -1.5708
    c: Coincident(g3,g-5)
    c: Vertical(g3)
    c: Coincident(g4,g2)
    c: Vertical(g4)
    c: Coincident(g5,g3)
    c: Coincident(g5,g4)
    c: Horizontal(g5)
    c: DistanceY(g3,g3) = 0.7
FEATURE [PartDesign::Pocket] Pocket161
  BaseFeature = -> Pocket159
  Direction = (0,0,1)
  Length = 0.2
  Length2 = 5
  Profile = -> Sketch371
  ReferenceAxis = -> Sketch371 [N_Axis]
  Refine = true
  Suppressed = false
  Type = 0
FEATURE [Sketcher::SketchObject] Sketch372
  ArcFitTolerance = 1e-06
  AttachmentSupport = -> [Pocket161]
  ExternalGeometry = -> [Pocket161]
  FullyConstrained = true
  MakeInternals = false
  MapMode = 5
  Placement = pos=(0,0,31.4) rot=(0,0,1;0rad)
  sketch-geometry (6):
    g0: LineSegment StartX=-8.02561 StartY=-13.8169 StartZ=0 EndX=-5.72778 EndY=-13.8169 EndZ=0
    g1: ArcOfCircle CenterX=-6.8767 CenterY=-13.0169 CenterZ=0 NormalX=0 NormalY=0 NormalZ=1 AngleXU=0 Radius=1.4 StartAngle=3.12949 EndAngle=3.74983
    g2: ArcOfCircle CenterX=-6.8767 CenterY=-13.0169 CenterZ=0 NormalX=0 NormalY=0 NormalZ=1 AngleXU=0 Radius=1.4 StartAngle=5.67495 EndAngle=6.29528
    g3: LineSegment StartX=-8.27659 StartY=-13 StartZ=0 EndX=-8.27659 EndY=-12.3 EndZ=0
    g4: LineSegment StartX=-5.4768 StartY=-13 StartZ=0 EndX=-5.4768 EndY=-12.3 EndZ=0
    g5: LineSegment StartX=-5.4768 StartY=-12.3 StartZ=0 EndX=-8.27659 EndY=-12.3 EndZ=0
  constraints (14):
    c: Coincident(g0,g-5)
    c: Coincident(g0,g-5)
    c: Coincident(g1,g0)
    c: Tangent(g1,g-4) = -1.5708
    c: Coincident(g2,g0)
    c: Tangent(g2,g-3) = -1.5708
    c: Coincident(g3,g1)
    c: Vertical(g3)
    c: Coincident(g4,g2)
    c: Vertical(g4)
    c: Coincident(g5,g4)
    c: Coincident(g5,g3)
    c: Horizontal(g5)
    c: DistanceY(g3,g3) = 0.7
FEATURE [PartDesign::Pocket] Pocket162
  BaseFeature = -> Pocket161
  Direction = (0,0,-1)
  Length = 0.2
  Length2 = 5
  Profile = -> Sketch372
  ReferenceAxis = -> Sketch372 [N_Axis]
  Refine = true
  Suppressed = false
  Type = 0
FEATURE [PartDesign::Body] Body016  label="Roof"
  AllowCompound = false
  Group = -> [Sketch335,Pad198,Sketch336,Pocket141,Sketch337,Pocket142,Sketch338,Pocket143,Sketch339,Pocket144,Sketch340,Pocket145,Sketch341,Pad199,Sketch342,Pad200,Sketch343,Pocket146,Sketch344,Pad201,Sketch345,Pad202,Sketch346,Pad203,Sketch347,Pocket147,Sketch348,Pocket148,Sketch349,Pocket149,Sketch366,Pocket156,Pocket157,Sketch367,Pocket158,Sketch369,Pocket159,Sketch371,Pocket161,Sketch372,Pocket162,+2 more]
  Origin = -> Origin017
  Placement = pos=(-20,17,25.6) rot=(1,0,0;1.5708rad)
  Tip = -> Pocket163
COMPONENT P8 — recipe-attached ("Smoke_Stack", modeled in this document).
Construction recipe (the document's own serialized feature program — sketch geometry with constraints, then the solid features built on it; lengths are millimeters unless a unit is written):

FEATURE [PartDesign::SubShapeBinder] Binder007
  BindCopyOnChange = 0
  BindMode = 2
  ClaimChildren = false
  Context = -> Body018 [Binder007.]
  Fuse = false
  MakeFace = true
  OffsetFill = false
  OffsetIntersection = false
  OffsetJoinType = 0
  OffsetOpenResult = false
  PartialLoad = false
  Refine = true
  Relative = true
  _Version = 2
FEATURE [Sketcher::SketchObject] Sketch350
  ArcFitTolerance = 1e-06
  AttachmentSupport = -> [Binder007]
  ExternalGeometry = -> [Binder007]
  FullyConstrained = true
  MakeInternals = false
  MapMode = 5
  Placement = pos=(0,0,11.6) rot=(0,0,1;0rad)
  sketch-geometry (4):
    g0: LineSegment StartX=-20 StartY=-7.5 StartZ=0 EndX=-20 EndY=-16.1 EndZ=0
    g1: LineSegment StartX=-20 StartY=-16.1 StartZ=0 EndX=-11.4 EndY=-16.1 EndZ=0
    g2: LineSegment StartX=-11.4 StartY=-16.1 StartZ=0 EndX=-11.4 EndY=-7.5 EndZ=0
    g3: LineSegment StartX=-11.4 StartY=-7.5 StartZ=0 EndX=-20 EndY=-7.5 EndZ=0
  constraints (13):
    c: DistanceY(g-7,g-7) = 6
    c: Vertical(g0)
    c: Coincident(g1,g0)
    c: Horizontal(g1)
    c: Coincident(g2,g1)
    c: Vertical(g2)
    c: Coincident(g3,g2)
    c: Coincident(g3,g0)
    c: Horizontal(g3)
    c: DistanceX(g0,g-7) = 1.3
    c: DistanceY(g-7,g0) = 1.3
    c: DistanceY(g0,g-7) = 1.3
    c: DistanceX(g-6,g1) = 1.3
FEATURE [PartDesign::Pad] Pad204
  Direction = (0,0,1)
  Length = 4.8
  Length2 = 10
  Profile = -> Sketch350
  ReferenceAxis = -> Sketch350 [N_Axis]
  Refine = true
  Suppressed = false
  Type = 0
FEATURE [Sketcher::SketchObject] Sketch351
  ArcFitTolerance = 1e-06
  AttachmentSupport = -> [Pad204]
  ExternalGeometry = -> [Binder007,Pad204]
  FullyConstrained = true
  MakeInternals = false
  MapMode = 5
  Placement = pos=(-11.4,0,0) rot=(0.57735,0.57735,0.57735;2.0944rad)
  sketch-geometry (2):
    g0: Circle CenterX=-13.5 CenterY=13.3 CenterZ=0 NormalX=0 NormalY=0 NormalZ=1 AngleXU=0 Radius=1.7
    g1: Circle CenterX=-10.1 CenterY=13.3 CenterZ=0 NormalX=0 NormalY=0 NormalZ=1 AngleXU=0 Radius=1.7
  constraints (8):
    c: Diameter(g1) = 3.4
    c: Diameter(g0) = 3.4
    c: Tangent(g1,g0)
    c: DistanceY(g0,g1) = 0
    c: Tangent(g0,g-3)
    c: DistanceX(g-6,g-6) = 8.6
    c: DistanceX(g-4,g0) = 2.6
    c: DistanceX(g1,g-5) = 2.6
FEATURE [PartDesign::Pad] Pad205
  BaseFeature = -> Pad204
  Direction = (1,0,0)
  Length = 8
  Length2 = 10
  Profile = -> Sketch351
  ReferenceAxis = -> Sketch351 [N_Axis]
  Refine = true
  Suppressed = false
  Type = 0
FEATURE [Sketcher::SketchObject] Sketch352
  ArcFitTolerance = 1e-06
  AttachmentSupport = -> [Pad205]
  ExternalGeometry = -> [Pad205,Binder007]
  FullyConstrained = true
  MakeInternals = false
  MapMode = 5
  Placement = pos=(-3.4,0,0) rot=(0.57735,0.57735,0.57735;2.0944rad)
  sketch-geometry (5):
    g0: LineSegment StartX=-11.8 StartY=13.3 StartZ=0 EndX=-15.2 EndY=13.3 EndZ=0
    g1: LineSegment StartX=-11.8 StartY=13.3 StartZ=0 EndX=-8.4 EndY=13.3 EndZ=0
    g2: LineSegment StartX=-8.4 StartY=13.3 StartZ=0 EndX=-8.4 EndY=11.6 EndZ=0
    g3: LineSegment StartX=-15.2 StartY=13.3 StartZ=0 EndX=-15.2 EndY=11.6 EndZ=0
    g4: LineSegment StartX=-15.2 StartY=11.6 StartZ=0 EndX=-8.4 EndY=11.6 EndZ=0
  constraints (13):
    c: Coincident(g0,g-3)
    c: PointOnObject(g0,g-4)
    c: Horizontal(g0)
    c: Coincident(g1,g0)
    c: Coincident(g1,g-3)
    c: Vertical(g2)
    c: PointOnObject(g2,g-5)
    c: Coincident(g2,g1)
    c: Vertical(g3)
    c: PointOnObject(g3,g-5)
    c: Coincident(g3,g0)
    c: Coincident(g4,g3)
    c: Coincident(g4,g2)
FEATURE [PartDesign::Pad] Pad206
  BaseFeature = -> Pad205
  Direction = (1,0,0)
  Length = 8
  Length2 = 10
  Profile = -> Sketch352
  ReferenceAxis = -> Sketch352 [N_Axis]
  Refine = true
  Reversed = true
  Suppressed = false
  Type = 0
FEATURE [Sketcher::SketchObject] Sketch353
  ArcFitTolerance = 1e-06
  AttachmentSupport = -> [Pad206]
  ExternalGeometry = -> [Pad206]
  FullyConstrained = true
  MakeInternals = false
  MapMode = 5
  Placement = pos=(0,0,16.4) rot=(0,0,1;0rad)
  sketch-geometry (1):
    g0: Circle CenterX=-15.7 CenterY=-11.8 CenterZ=0 NormalX=0 NormalY=0 NormalZ=1 AngleXU=0 Radius=3.25
  constraints (5):
    c: Diameter(g0) = 6.5
    c: DistanceX(g-3,g-3) = 8.6
    c: DistanceY(g-4,g-4) = 8.6
    c: DistanceX(g-4,g0) = 4.3
    c: DistanceY(g0,g-4) = 4.3
FEATURE [PartDesign::Pad] Pad207
  BaseFeature = -> Pad206
  Direction = (0,0,1)
  Length = 4.6
  Length2 = 10
  Profile = -> Sketch353
  ReferenceAxis = -> Sketch353 [N_Axis]
  Refine = true
  Suppressed = false
  Type = 0
FEATURE [Sketcher::SketchObject] Sketch354
  ArcFitTolerance = 1e-06
  AttachmentSupport = -> [Pad207]
  ExternalGeometry = -> [Pad207]
  FullyConstrained = true
  MakeInternals = false
  MapMode = 5
  Placement = pos=(0,0,21) rot=(0,0,1;0rad)
  sketch-geometry (1):
    g0: Circle CenterX=-15.7 CenterY=-11.8 CenterZ=0 NormalX=0 NormalY=0 NormalZ=1 AngleXU=0 Radius=2.5
  constraints (2):
    c: Coincident(g0,g-3)
    c: Diameter(g0) = 5
FEATURE [PartDesign::Pad] Pad208
  BaseFeature = -> Pad207
  Direction = (0,0,1)
  Length = 4
  Length2 = 10
  Profile = -> Sketch354
  ReferenceAxis = -> Sketch354 [N_Axis]
  Refine = true
  Suppressed = false
  Type = 0
FEATURE [Sketcher::SketchObject] Sketch355
  ArcFitTolerance = 1e-06
  AttachmentSupport = -> [Pad208]
  ExternalGeometry = -> [Pad208]
  FullyConstrained = true
  MakeInternals = false
  MapMode = 5
  Placement = pos=(0,0,25) rot=(0,0,1;0rad)
  sketch-geometry (1):
    g0: Circle CenterX=-15.7 CenterY=-11.8 CenterZ=0 NormalX=0 NormalY=0 NormalZ=1 AngleXU=0 Radius=0.75
  constraints (2):
    c: Coincident(g0,g-3)
    c: Diameter(g0) = 1.5
FEATURE [PartDesign::Pocket] Pocket150
  BaseFeature = -> Pad208
  Direction = (0,0,-1)
  Length = 14
  Length2 = 5
  Profile = -> Sketch355
  ReferenceAxis = -> Sketch355 [N_Axis]
  Refine = true
  Suppressed = false
  Type = 0
FEATURE [PartDesign::Fillet] Fillet022
  Base = -> Pocket150 [Edge10,Edge2,Edge8,Edge17,Edge7,Edge4,Edge32,Edge34,Edge5,Edge1,Edge28,Edge27,Edge24,Edge26]
  BaseFeature = -> Pocket150
  Radius = 0.5
  Refine = true
  SupportTransform = false
  Suppressed = false
  UseAllEdges = false
FEATURE [Sketcher::SketchObject] Sketch356
  ArcFitTolerance = 1e-06
  AttachmentSupport = -> [Binder007]
  ExternalGeometry = -> [Binder007]
  FullyConstrained = true
  MakeInternals = false
  MapMode = 5
  Placement = pos=(0,0,11.6) rot=(0,0,1;0rad)
  sketch-geometry (1):
    g0: Circle CenterX=-5.8 CenterY=-11.8 CenterZ=0 NormalX=0 NormalY=0 NormalZ=1 AngleXU=0 Radius=0.65
  constraints (2):
    c: Coincident(g0,g-3)
    c: Equal(g0,g-3)
FEATURE [PartDesign::Pad] Pad209
  BaseFeature = -> Fillet022
  Direction = (0,0,1)
  Length = 1.3
  Length2 = 10
  Profile = -> Sketch356
  ReferenceAxis = -> Sketch356 [N_Axis]
  Refine = true
  Reversed = true
  Suppressed = false
  Type = 0
FEATURE [Sketcher::SketchObject] Sketch357
  ArcFitTolerance = 1e-06
  AttachmentSupport = -> [Pad209]
  ExternalGeometry = -> [Binder007]
  FullyConstrained = true
  MakeInternals = false
  MapMode = 5
  Placement = pos=(-4.3e-15,0,11.6) rot=(1,0,0;3.14159rad)
  sketch-geometry (4):
    g0: LineSegment StartX=-18.7 StartY=14.8 StartZ=0 EndX=-18.7 EndY=8.8 EndZ=0
    g1: LineSegment StartX=-18.7 StartY=8.8 StartZ=0 EndX=-12.7 EndY=8.8 EndZ=0
    g2: LineSegment StartX=-12.7 StartY=8.8 StartZ=0 EndX=-12.7 EndY=14.8 EndZ=0
    g3: LineSegment StartX=-12.7 StartY=14.8 StartZ=0 EndX=-18.7 EndY=14.8 EndZ=0
  constraints (10):
    c: Coincident(g0,g1)
    c: Coincident(g1,g2)
    c: Coincident(g2,g3)
    c: Coincident(g3,g0)
    c: Vertical(g0)
    c: Vertical(g2)
    c: Horizontal(g1)
    c: Horizontal(g3)
    c: Coincident(g0,g-6)
    c: Coincident(g1,g-5)
FEATURE [PartDesign::Pocket] Pocket151
  BaseFeature = -> Pad209
  Direction = (0,0,1)
  Length = 3
  Length2 = 5
  Profile = -> Sketch357
  ReferenceAxis = -> Sketch357 [N_Axis]
  Refine = true
  Suppressed = false
  Type = 0
FEATURE [Sketcher::SketchObject] Sketch358
  ArcFitTolerance = 1e-06
  AttachmentSupport = -> [Pocket151]
  ExternalGeometry = -> [Pocket151]
  FullyConstrained = true
  MakeInternals = false
  MapMode = 5
  Placement = pos=(0,0,14.6) rot=(1,0,0;3.14159rad)
  sketch-geometry (2):
    g0: Circle CenterX=-15.7 CenterY=11.8 CenterZ=0 NormalX=0 NormalY=0 NormalZ=1 AngleXU=0 Radius=2.5
    g1: Circle CenterX=-15.7 CenterY=11.8 CenterZ=0 NormalX=0 NormalY=0 NormalZ=1 AngleXU=0 Radius=0.750005
  constraints (4):
    c: Coincident(g0,g-3)
    c: Diameter(g0) = 5
    c: Coincident(g1,g0)
    c: Tangent(g1,g-3)
FEATURE [PartDesign::Pad] Pad210
  BaseFeature = -> Pocket151
  Direction = (0,0,-1)
  Length = 1.5
  Length2 = 10
  Profile = -> Sketch358
  ReferenceAxis = -> Sketch358 [N_Axis]
  Refine = true
  Suppressed = false
  Type = 0
FEATURE [Sketcher::SketchObject] Sketch359
  ArcFitTolerance = 1e-06
  AttachmentSupport = -> [Pad210]
  ExternalGeometry = -> [Pad210]
  FullyConstrained = true
  MakeInternals = false
  MapMode = 5
  Placement = pos=(-4.3e-15,0,11.6) rot=(1,0,0;3.14159rad)
  sketch-geometry (4):
    g0: LineSegment StartX=-12.7 StartY=14.2 StartZ=0 EndX=-12.7 EndY=9.4 EndZ=0
    g1: LineSegment StartX=-12.7 StartY=9.4 StartZ=0 EndX=-6.45 EndY=9.4 EndZ=0
    g2: LineSegment StartX=-6.45 StartY=9.4 StartZ=0 EndX=-6.45 EndY=14.2 EndZ=0
    g3: LineSegment StartX=-6.45 StartY=14.2 StartZ=0 EndX=-12.7 EndY=14.2 EndZ=0
  constraints (12):
    c: Coincident(g0,g1)
    c: Coincident(g1,g2)
    c: Coincident(g2,g3)
    c: Coincident(g3,g0)
    c: Vertical(g0)
    c: Vertical(g2)
    c: Horizontal(g1)
    c: Horizontal(g3)
    c: PointOnObject(g0,g-4)
    c: Tangent(g2,g-6)
    c: DistanceY(g-8,g1) = 1
    c: DistanceY(g2,g-7) = 1
FEATURE [PartDesign::Pocket] Pocket152
  BaseFeature = -> Pad210
  Direction = (0,0,1)
  Length = 1.5
  Length2 = 5
  Profile = -> Sketch359
  ReferenceAxis = -> Sketch359 [N_Axis]
  Refine = true
  Suppressed = false
  Type = 0
FEATURE [Sketcher::SketchObject] Sketch360
  ArcFitTolerance = 1e-06
  AttachmentSupport = -> [Pocket152]
  ExternalGeometry = -> [Pocket152]
  FullyConstrained = true
  MakeInternals = false
  MapMode = 5
  Placement = pos=(-4.3e-15,0,11.6) rot=(1,0,0;3.14159rad)
  sketch-geometry (5):
    g0: LineSegment StartX=-6.45 StartY=11.8 StartZ=0 EndX=-6.45 EndY=14.2 EndZ=0
    g1: LineSegment StartX=-6.45 StartY=14.2 StartZ=0 EndX=-4.4 EndY=14.2 EndZ=0
    g2: ArcOfCircle CenterX=-5.8 CenterY=11.8 CenterZ=0 NormalX=0 NormalY=0 NormalZ=1 AngleXU=0 Radius=0.65 StartAngle=0 EndAngle=3.14159
    g3: LineSegment StartX=-5.15 StartY=11.8 StartZ=0 EndX=-4.4 EndY=11.8 EndZ=0
    g4: LineSegment StartX=-4.4 StartY=11.8 StartZ=0 EndX=-4.4 EndY=14.2 EndZ=0
  constraints (12):
    c: Coincident(g0,g-6)
    c: Coincident(g0,g-5)
    c: Coincident(g1,g0)
    c: Horizontal(g1)
    c: DistanceX(g1,g-4) = 1
    c: Coincident(g2,g0)
    c: Tangent(g2,g-3) = -1.5708
    c: Coincident(g3,g2)
    c: Horizontal(g3)
    c: Coincident(g4,g3)
    c: Coincident(g4,g1)
    c: Vertical(g4)
FEATURE [PartDesign::Pocket] Pocket153
  BaseFeature = -> Pocket152
  Direction = (0,0,1)
  Length = 1.5
  Length2 = 5
  Profile = -> Sketch360
  ReferenceAxis = -> Sketch360 [N_Axis]
  Refine = true
  Suppressed = false
  Type = 0
FEATURE [Sketcher::SketchObject] Sketch361
  ArcFitTolerance = 1e-06
  AttachmentSupport = -> [Pocket153]
  ExternalGeometry = -> [Pocket153]
  FullyConstrained = true
  MakeInternals = false
  MapMode = 5
  Placement = pos=(-4.3e-15,0,11.6) rot=(1,0,0;3.14159rad)
  sketch-geometry (5):
    g0: ArcOfCircle CenterX=-5.8 CenterY=11.8 CenterZ=0 NormalX=0 NormalY=0 NormalZ=1 AngleXU=0 Radius=0.65 StartAngle=3.14158 EndAngle=6.28319
    g1: LineSegment StartX=-5.15 StartY=11.8 StartZ=0 EndX=-4.4 EndY=11.8 EndZ=0
    g2: LineSegment StartX=-4.4 StartY=11.8 StartZ=0 EndX=-4.4 EndY=9.4 EndZ=0
    g3: LineSegment StartX=-6.45 StartY=9.4 StartZ=0 EndX=-4.4 EndY=9.4 EndZ=0
    g4: LineSegment StartX=-6.45 StartY=11.8 StartZ=0 EndX=-6.45 EndY=9.4 EndZ=0
  constraints (12):
    c: Coincident(g0,g-5)
    c: Coincident(g0,g-4)
    c: Coincident(g1,g0)
    c: Coincident(g1,g-5)
    c: Coincident(g2,g1)
    c: Vertical(g2)
    c: Coincident(g3,g-4)
    c: Coincident(g3,g2)
    c: Horizontal(g3)
    c: Coincident(g4,g0)
    c: Coincident(g4,g3)
    c: Tangent(g0,g-3)
FEATURE [PartDesign::Pocket] Pocket154
  BaseFeature = -> Pocket153
  Direction = (0,0,1)
  Length = 1.5
  Length2 = 5
  Profile = -> Sketch361
  ReferenceAxis = -> Sketch361 [N_Axis]
  Refine = true
  Suppressed = false
  Type = 0
FEATURE [Sketcher::SketchObject] Sketch362
  ArcFitTolerance = 1e-06
  AttachmentSupport = -> [Pocket154]
  ExternalGeometry = -> [Pocket154]
  FullyConstrained = true
  MakeInternals = false
  MapMode = 5
  Placement = pos=(0,0,13.1) rot=(1,0,0;3.14159rad)
  sketch-geometry (4):
    g0: LineSegment StartX=-12.7 StartY=12.45 StartZ=0 EndX=-12.7 EndY=11.15 EndZ=0
    g1: LineSegment StartX=-12.7 StartY=11.15 StartZ=0 EndX=-4.4 EndY=11.15 EndZ=0
    g2: LineSegment StartX=-4.4 StartY=11.15 StartZ=0 EndX=-4.4 EndY=12.45 EndZ=0
    g3: LineSegment StartX=-4.4 StartY=12.45 StartZ=0 EndX=-12.7 EndY=12.45 EndZ=0
  constraints (12):
    c: Coincident(g0,g1)
    c: Coincident(g1,g2)
    c: Coincident(g2,g3)
    c: Coincident(g3,g0)
    c: Vertical(g0)
    c: Vertical(g2)
    c: Horizontal(g1)
    c: Horizontal(g3)
    c: PointOnObject(g0,g-4)
    c: PointOnObject(g1,g-3)
    c: Tangent(g3,g-5)
    c: Tangent(g1,g-5)
FEATURE [PartDesign::Pad] Pad211
  BaseFeature = -> Pocket154
  Direction = (0,0,-1)
  Length = 0.5
  Length2 = 10
  Profile = -> Sketch362
  ReferenceAxis = -> Sketch362 [N_Axis]
  Refine = true
  Suppressed = false
  Type = 0
FEATURE [Sketcher::SketchObject] Sketch422
  ArcFitTolerance = 1e-06
  AttachmentSupport = -> [Pad211]
  ExternalGeometry = -> [Pad211]
  FullyConstrained = false
  MakeInternals = false
  MapMode = 5
  Placement = pos=(0,0,10.3) rot=(1,0,0;3.14159rad)
  sketch-geometry (2):
    g0: Circle CenterX=-5.8 CenterY=11.8 CenterZ=0 NormalX=0 NormalY=0 NormalZ=1 AngleXU=0 Radius=0.6
    g1: Circle CenterX=-5.8 CenterY=11.8 CenterZ=0 NormalX=0 NormalY=0 NormalZ=1 AngleXU=0 Radius=0.808858
  constraints (2):
    c: Radius(g0) = 0.6
    c: Coincident(g1,g0)
FEATURE [PartDesign::Pocket] Pocket195
  BaseFeature = -> Pad211
  Direction = (0,0,1)
  Length = 2.3
  Length2 = 5
  Profile = -> Sketch422
  ReferenceAxis = -> Sketch422 [N_Axis]
  Refine = true
  Suppressed = false
  Type = 0
FEATURE [PartDesign::Body] Body018  label="Smoke_Stack"
  AllowCompound = false
  Group = -> [Binder007,Sketch350,Pad204,Sketch351,Pad205,Sketch352,Pad206,Sketch353,Pad207,Sketch354,Pad208,Sketch355,Pocket150,Fillet022,Sketch356,Pad209,Sketch357,Pocket151,Sketch358,Pad210,Sketch359,Pocket152,Sketch360,Pocket153,Sketch361,Pocket154,Sketch362,Pad211,Sketch422,Pocket195]
  Origin = -> Origin019
  Tip = -> Pocket195
COMPONENT P9 — recipe-attached ("Waist_Filler", modeled in this document).
Construction recipe (the document's own serialized feature program — sketch geometry with constraints, then the solid features built on it; lengths are millimeters unless a unit is written):

FEATURE [PartDesign::SubShapeBinder] Binder008
  BindCopyOnChange = 0
  BindMode = 2
  ClaimChildren = false
  Context = -> Body019 [Binder008.]
  Fuse = false
  MakeFace = true
  OffsetFill = false
  OffsetIntersection = false
  OffsetJoinType = 0
  OffsetOpenResult = false
  PartialLoad = false
  Refine = true
  Relative = true
  _Version = 2
FEATURE [Sketcher::SketchObject] Sketch374
  ArcFitTolerance = 1e-06
  AttachmentSupport = -> [Binder008]
  ExternalGeometry = -> [Binder008]
  FullyConstrained = true
  MakeInternals = false
  MapMode = 5
  Placement = pos=(0,0,3.4) rot=(1,0,0;3.14159rad)
  sketch-geometry (8):
    g0: LineSegment StartX=-26.1 StartY=4 StartZ=0 EndX=-26.1 EndY=-4 EndZ=0
    g1: LineSegment StartX=-26.1 StartY=-4 StartZ=0 EndX=-8.5 EndY=-4 EndZ=0
    g2: LineSegment StartX=-8.5 StartY=-4 StartZ=0 EndX=-8.5 EndY=4 EndZ=0
    g3: LineSegment StartX=-8.5 StartY=4 StartZ=0 EndX=-26.1 EndY=4 EndZ=0
    g4: LineSegment StartX=-24.6 StartY=2.5 StartZ=0 EndX=-10 EndY=2.5 EndZ=0
    g5: LineSegment StartX=-10 StartY=2.5 StartZ=0 EndX=-10 EndY=-2.5 EndZ=0
    g6: LineSegment StartX=-10 StartY=-2.5 StartZ=0 EndX=-24.6 EndY=-2.5 EndZ=0
    g7: LineSegment StartX=-24.6 StartY=-2.5 StartZ=0 EndX=-24.6 EndY=2.5 EndZ=0
  constraints (21):
    c: DistanceX(g-3,g-3) = 17.6
    c: Coincident(g0,g-8)
    c: Coincident(g0,g-8)
    c: Coincident(g1,g0)
    c: Coincident(g1,g-5)
    c: Coincident(g2,g1)
    c: Coincident(g2,g-4)
    c: Coincident(g3,g2)
    c: Coincident(g3,g0)
    c: Horizontal(g4)
    c: Vertical(g5)
    c: Coincident(g6,g5)
    c: Horizontal(g6)
    c: Coincident(g7,g6)
    c: Coincident(g7,g4)
    c: Vertical(g7)
    c: DistanceY(g4,g0) = 1.5
    c: DistanceY(g0,g6) = 1.5
    c: Coincident(g4,g5)
    c: DistanceX(g0,g4) = 1.5
    c: DistanceX(g4,g2) = 1.5
FEATURE [PartDesign::Pad] Pad214
  Direction = (0,0,-1)
  Length = 3.7
  Length2 = 10
  Profile = -> Sketch374
  ReferenceAxis = -> Sketch374 [N_Axis]
  Refine = true
  Suppressed = false
  Type = 0
FEATURE [Sketcher::SketchObject] Sketch375
  ArcFitTolerance = 1e-06
  AttachmentSupport = -> [Pad214]
  ExternalGeometry = -> [Pad214]
  FullyConstrained = true
  MakeInternals = false
  MapMode = 5
  Placement = pos=(0,-4,0) rot=(1,0,0;1.5708rad)
  sketch-geometry (4):
    g0: LineSegment StartX=-26.1 StartY=-0.3 StartZ=0 EndX=-8.5 EndY=-0.3 EndZ=0
    g1: LineSegment StartX=-26.1 StartY=-0.3 StartZ=0 EndX=-21.6 EndY=-4.8 EndZ=0
    g2: LineSegment StartX=-21.6 StartY=-4.8 StartZ=0 EndX=-8.5 EndY=-4.8 EndZ=0
    g3: LineSegment StartX=-8.5 StartY=-0.3 StartZ=0 EndX=-8.5 EndY=-4.8 EndZ=0
  constraints (10):
    c: Coincident(g0,g-3)
    c: Coincident(g0,g-3)
    c: Coincident(g1,g0)
    c: Coincident(g2,g1)
    c: Horizontal(g2)
    c: Coincident(g3,g0)
    c: Coincident(g3,g2)
    c: Vertical(g3)
    c: Angle(g1,g0) = 0.785398
    c: DistanceY(g3,g3) = 4.5
FEATURE [PartDesign::Pad] Pad215
  BaseFeature = -> Pad214
  Direction = (0,-1,2e-16)
  Length = 8
  Length2 = 10
  Profile = -> Sketch375
  ReferenceAxis = -> Sketch375 [N_Axis]
  Refine = true
  Reversed = true
  Suppressed = false
  Type = 0
FEATURE [Sketcher::SketchObject] Sketch376
  ArcFitTolerance = 1e-06
  AttachmentSupport = -> [Binder008]
  ExternalGeometry = -> [Binder008]
  FullyConstrained = true
  MakeInternals = false
  MapMode = 5
  Placement = pos=(0,0,3.4) rot=(1,0,0;3.14159rad)
  sketch-geometry (2):
    g0: Circle CenterX=-23.6 CenterY=0 CenterZ=0 NormalX=0 NormalY=0 NormalZ=1 AngleXU=0 Radius=0.5
    g1: Circle CenterX=-9.675 CenterY=0 CenterZ=0 NormalX=0 NormalY=0 NormalZ=1 AngleXU=0 Radius=0.9
  constraints (4):
    c: Coincident(g0,g-5)
    c: Equal(g0,g-5)
    c: Coincident(g1,g-3)
    c: Equal(g1,g-3)
FEATURE [PartDesign::Pad] Pad216
  BaseFeature = -> Pad215
  Direction = (0,0,-1)
  Length = 5
  Length2 = 10
  Profile = -> Sketch376
  ReferenceAxis = -> Sketch376 [N_Axis]
  Refine = true
  Suppressed = false
  Type = 0
FEATURE [PartDesign::Pad] Pad217
  BaseFeature = -> Pad216
  Direction = (0,0,-1)
  Length = 1.5
  Length2 = 10
  Profile = -> Sketch376
  ReferenceAxis = -> Sketch376 [N_Axis]
  Refine = true
  Reversed = true
  Suppressed = false
  Type = 0
FEATURE [Sketcher::SketchObject] Sketch377
  ArcFitTolerance = 1e-06
  AttachmentSupport = -> [Pad217]
  ExternalGeometry = -> [Pad217]
  FullyConstrained = false
  MakeInternals = false
  MapMode = 5
  Placement = pos=(0,0,3.4) rot=(0,0,1;0rad)
  sketch-geometry (4):
    g0: LineSegment StartX=-24.6 StartY=2.5 StartZ=0 EndX=-24.6 EndY=-2.5 EndZ=0
    g1: LineSegment StartX=-24.6 StartY=-2.5 StartZ=0 EndX=-22.6997 EndY=-2.5 EndZ=0
    g2: LineSegment StartX=-22.6997 StartY=-2.5 StartZ=0 EndX=-22.6997 EndY=2.5 EndZ=0
    g3: LineSegment StartX=-22.6997 StartY=2.5 StartZ=0 EndX=-24.6 EndY=2.5 EndZ=0
  constraints (10):
    c: Coincident(g0,g1)
    c: Coincident(g1,g2)
    c: Coincident(g2,g3)
    c: Coincident(g3,g0)
    c: Vertical(g0)
    c: Vertical(g2)
    c: Horizontal(g1)
    c: Horizontal(g3)
    c: Coincident(g0,g-3)
    c: PointOnObject(g1,g-4)
FEATURE [PartDesign::Pad] Pad218
  BaseFeature = -> Pad217
  Direction = (0,0,1)
  Length = 5
  Length2 = 10
  Profile = -> Sketch377
  ReferenceAxis = -> Sketch377 [N_Axis]
  Refine = true
  Reversed = true
  Suppressed = false
  Type = 0
FEATURE [PartDesign::Fillet] Fillet023
  Base = -> Pad218 [Edge10,Edge8,Edge14,Edge11,Edge7,Edge15,Edge12,Edge4,Edge6,Edge2,Edge1]
  BaseFeature = -> Pad218
  Radius = 0.5
  Refine = true
  SupportTransform = false
  Suppressed = false
  UseAllEdges = false
FEATURE [Sketcher::SketchObject] Sketch424
  ArcFitTolerance = 1e-06
  AttachmentSupport = -> [Fillet023]
  ExternalGeometry = -> [Fillet023]
  FullyConstrained = true
  MakeInternals = false
  MapMode = 5
  Placement = pos=(0,0,4.9) rot=(0,0,1;0rad)
  sketch-geometry (4):
    g0: Circle CenterX=-23.6 CenterY=0 CenterZ=0 NormalX=0 NormalY=0 NormalZ=1 AngleXU=0 Radius=0.5
    g1: Circle CenterX=-9.675 CenterY=0 CenterZ=0 NormalX=0 NormalY=0 NormalZ=1 AngleXU=0 Radius=0.9
    g2: Circle CenterX=-9.675 CenterY=0 CenterZ=0 NormalX=0 NormalY=0 NormalZ=1 AngleXU=0 Radius=0.85
    g3: Circle CenterX=-23.6 CenterY=0 CenterZ=0 NormalX=0 NormalY=0 NormalZ=1 AngleXU=0 Radius=0.45
  constraints (10):
    c: Coincident(g0,g-4)
    c: Equal(g0,g-4)
    c: Coincident(g1,g-3)
    c: Equal(g1,g-3)
    c: Radius(g1) = 0.9
    c: Coincident(g2,g1)
    c: Radius(g2) = 0.85
    c: Radius(g0) = 0.5
    c: Coincident(g3,g0)
    c: Radius(g3) = 0.45
FEATURE [PartDesign::Pocket] Pocket197
  BaseFeature = -> Fillet023
  Direction = (0,0,-1)
  Length = 1.5
  Length2 = 5
  Profile = -> Sketch424
  ReferenceAxis = -> Sketch424 [N_Axis]
  Refine = true
  Suppressed = false
  Type = 0
FEATURE [PartDesign::Body] Body019  label="Waist_Filler"
  AllowCompound = false
  Group = -> [Binder008,Sketch374,Pad214,Sketch375,Pad215,Sketch376,Pad216,Pad217,Sketch377,Pad218,Fillet023,Sketch424,Pocket197]
  Origin = -> Origin020
  Tip = -> Pocket197
COMPONENT P10 — recipe-attached ("Cab", modeled in this document).
Construction recipe (the document's own serialized feature program — sketch geometry with constraints, then the solid features built on it; lengths are millimeters unless a unit is written):

FEATURE [PartDesign::SubShapeBinder] Binder009
  BindCopyOnChange = 0
  BindMode = 2
  ClaimChildren = false
  Context = -> Body020 [Binder009.]
  Fuse = false
  MakeFace = true
  OffsetFill = false
  OffsetIntersection = false
  OffsetJoinType = 0
  OffsetOpenResult = false
  PartialLoad = false
  Refine = true
  Relative = true
  _Version = 2
FEATURE [Sketcher::SketchObject] Sketch378
  ArcFitTolerance = 1e-06
  AttachmentSupport = -> [Binder009]
  ExternalGeometry = -> [Binder009]
  FullyConstrained = true
  MakeInternals = false
  MapMode = 5
  Placement = pos=(0,0,11.6) rot=(0,0,1;0rad)
  sketch-geometry (20):
    g0: LineSegment StartX=-18.7 StartY=17 StartZ=0 EndX=-18.7 EndY=7.2 EndZ=0
    g1: ArcOfCircle CenterX=-18.2 CenterY=7.2 CenterZ=0 NormalX=0 NormalY=0 NormalZ=1 AngleXU=0 Radius=0.5 StartAngle=3.14159 EndAngle=4.71239
    g2: LineSegment StartX=-18.2 StartY=6.7 StartZ=0 EndX=-16.4 EndY=6.7 EndZ=0
    g3: LineSegment StartX=-16.4 StartY=6.7 StartZ=0 EndX=-16.4 EndY=5.2 EndZ=0
    g4: LineSegment StartX=-16.4 StartY=5.2 StartZ=0 EndX=-6.1 EndY=5.2 EndZ=0
    g5: LineSegment StartX=-6.1 StartY=5.2 StartZ=0 EndX=-6.1 EndY=6.7 EndZ=0
    g6: LineSegment StartX=-6.1 StartY=6.7 StartZ=0 EndX=-0.3 EndY=6.7 EndZ=0
    g7: ArcOfCircle CenterX=-0.3 CenterY=7.2 CenterZ=0 NormalX=0 NormalY=0 NormalZ=1 AngleXU=0 Radius=0.5 StartAngle=4.71239 EndAngle=6.28319
    g8: LineSegment StartX=0.2 StartY=7.2 StartZ=0 EndX=0.2 EndY=17 EndZ=0
    g9: ArcOfCircle CenterX=-0.3 CenterY=17 CenterZ=0 NormalX=0 NormalY=0 NormalZ=1 AngleXU=0 Radius=0.5 StartAngle=0 EndAngle=1.5708
    g10: LineSegment StartX=-0.3 StartY=17.5 StartZ=0 EndX=-18.2 EndY=17.5 EndZ=0
    g11: ArcOfCircle CenterX=-18.2 CenterY=17 CenterZ=0 NormalX=0 NormalY=0 NormalZ=1 AngleXU=0 Radius=0.5 StartAngle=1.5708 EndAngle=3.14159
    g12: LineSegment StartX=-17.2 StartY=8.2 StartZ=0 EndX=-17.2 EndY=16 EndZ=0
    g13: LineSegment StartX=-17.2 StartY=16 StartZ=0 EndX=-1.3 EndY=16 EndZ=0
    g14: LineSegment StartX=-1.3 StartY=16 StartZ=0 EndX=-1.3 EndY=8.2 EndZ=0
    g15: LineSegment StartX=-1.3 StartY=8.2 StartZ=0 EndX=-7.3 EndY=8.2 EndZ=0
    g16: LineSegment StartX=-7.3 StartY=8.2 StartZ=0 EndX=-7.3 EndY=6.4 EndZ=0
    g17: LineSegment StartX=-7.3 StartY=6.4 StartZ=0 EndX=-15.2 EndY=6.4 EndZ=0
    g18: LineSegment StartX=-15.2 StartY=6.4 StartZ=0 EndX=-15.2 EndY=8.2 EndZ=0
    g19: LineSegment StartX=-15.2 StartY=8.2 StartZ=0 EndX=-17.2 EndY=8.2 EndZ=0
  constraints (66):
    c: PointOnObject(g0,g-17)
    c: Vertical(g0)
    c: Coincident(g1,g0)
    c: Coincident(g2,g1)
    c: Horizontal(g2)
    c: Coincident(g3,g2)
    c: Vertical(g3)
    c: Coincident(g4,g3)
    c: Horizontal(g4)
    c: Coincident(g5,g4)
    c: Vertical(g5)
    c: Coincident(g6,g5)
    c: Horizontal(g6)
    c: Coincident(g7,g6)
    c: Coincident(g8,g7)
    c: Vertical(g8)
    c: Coincident(g9,g8)
    c: Coincident(g10,g9)
    c: Horizontal(g10)
    c: Coincident(g11,g0)
    c: Coincident(g11,g10)
    c: PointOnObject(g-13,g8)
    c: DistanceY(g-13,g9) = 3
    c: DistanceY(g6,g-7) = 3
    c: DistanceY(g5,g5) = 1.5
    c: DistanceY(g7,g7) = 0
    c: DistanceY(g9,g8) = 0
    c: DistanceY(g0,g11) = 0
    c: Radius(g9) = 0.5
    c: Radius(g11) = 0.5
    c: Radius(g1) = 0.5
    c: Radius(g7) = 0.5
    c: DistanceY(g1,g0) = 0
    c: DistanceX(g1,g1) = 0
    c: DistanceX(g10,g11) = 0
    c: DistanceX(g9,g9) = 0
    c: DistanceX(g7,g6) = 0
    c: DistanceY(g1,g7) = 0
    c: DistanceX(g5,g7) = 6.3
    c: DistanceX(g4,g4) = 10.3
    c: DistanceX(g0,g2) = 2.3
    c: DistanceX(g-15,g-7) = 18.9
    c: Vertical(g12)
    c: Coincident(g13,g12)
    c: Horizontal(g13)
    c: Coincident(g14,g13)
    c: Vertical(g14)
    c: Coincident(g15,g14)
    c: Horizontal(g15)
    c: Coincident(g16,g15)
    c: Vertical(g16)
    c: Coincident(g17,g16)
    c: Horizontal(g17)
    c: Coincident(g18,g17)
    c: Vertical(g18)
    c: Coincident(g19,g18)
    c: Horizontal(g19)
    c: Coincident(g12,g19)
    c: DistanceY(g3,g17) = 1.2
    c: DistanceY(g13,g9) = 1.5
    c: DistanceY(g2,g12) = 1.5
    c: DistanceY(g5,g15) = 1.5
    c: DistanceX(g-17,g12) = 1.5
    c: DistanceX(g13,g8) = 1.5
    c: DistanceX(g16,g5) = 1.2
    c: DistanceX(g2,g17) = 1.2
FEATURE [PartDesign::Pad] Pad219
  Direction = (0,0,1)
  Length = 5.3
  Length2 = 10
  Profile = -> Sketch378
  ReferenceAxis = -> Sketch378 [N_Axis]
  Refine = true
  Suppressed = false
  Type = 0
FEATURE [Sketcher::SketchObject] Sketch379
  ArcFitTolerance = 1e-06
  AttachmentSupport = -> [Pad219]
  ExternalGeometry = -> [Pad219,Binder009]
  FullyConstrained = true
  MakeInternals = false
  MapMode = 5
  Placement = pos=(0,0,11.6) rot=(1,0,0;3.14159rad)
  sketch-geometry (4):
    g0: LineSegment StartX=-1.3 StartY=-9.7 StartZ=0 EndX=-1.3 EndY=-14.5 EndZ=0
    g1: LineSegment StartX=-1.3 StartY=-14.5 StartZ=0 EndX=2 EndY=-14.5 EndZ=0
    g2: LineSegment StartX=2 StartY=-14.5 StartZ=0 EndX=2 EndY=-9.7 EndZ=0
    g3: LineSegment StartX=2 StartY=-9.7 StartZ=0 EndX=-1.3 EndY=-9.7 EndZ=0
  constraints (12):
    c: Coincident(g0,g1)
    c: Coincident(g1,g2)
    c: Coincident(g2,g3)
    c: Coincident(g3,g0)
    c: Vertical(g0)
    c: Vertical(g2)
    c: Horizontal(g1)
    c: Horizontal(g3)
    c: PointOnObject(g0,g-3)
    c: DistanceX(g-4,g2) = 1.8
    c: PointOnObject(g-4,g3)
    c: PointOnObject(g-5,g1)
FEATURE [PartDesign::Pad] Pad220
  BaseFeature = -> Pad219
  Direction = (0,0,-1)
  Length = 1.5
  Length2 = 10
  Profile = -> Sketch379
  ReferenceAxis = -> Sketch379 [N_Axis]
  Refine = true
  Suppressed = false
  Type = 0
FEATURE [Sketcher::SketchObject] Sketch380
  ArcFitTolerance = 1e-06
  AttachmentSupport = -> [Pad220]
  ExternalGeometry = -> [Pad220]
  FullyConstrained = true
  MakeInternals = false
  MapMode = 5
  Placement = pos=(0,0,10.1) rot=(1,0,0;3.14159rad)
  sketch-geometry (8):
    g0: LineSegment StartX=-1.3 StartY=-9.7 StartZ=0 EndX=-1.3 EndY=-9.75 EndZ=0
    g1: LineSegment StartX=-1.3 StartY=-9.75 StartZ=0 EndX=2 EndY=-9.75 EndZ=0
    g2: LineSegment StartX=2 StartY=-9.75 StartZ=0 EndX=2 EndY=-9.7 EndZ=0
    g3: LineSegment StartX=2 StartY=-9.7 StartZ=0 EndX=-1.3 EndY=-9.7 EndZ=0
    g4: LineSegment StartX=-1.3 StartY=-14.5 StartZ=0 EndX=2 EndY=-14.5 EndZ=0
    g5: LineSegment StartX=2 StartY=-14.5 StartZ=0 EndX=2 EndY=-14.45 EndZ=0
    g6: LineSegment StartX=2 StartY=-14.45 StartZ=0 EndX=-1.3 EndY=-14.45 EndZ=0
    g7: LineSegment StartX=-1.3 StartY=-14.45 StartZ=0 EndX=-1.3 EndY=-14.5 EndZ=0
  constraints (22):
    c: Coincident(g0,g1)
    c: Coincident(g1,g2)
    c: Coincident(g2,g3)
    c: Coincident(g3,g0)
    c: Vertical(g0)
    c: Vertical(g2)
    c: Horizontal(g1)
    c: Horizontal(g3)
    c: Coincident(g0,g-5)
    c: PointOnObject(g1,g-4)
    c: Coincident(g4,g5)
    c: Coincident(g5,g6)
    c: Coincident(g6,g7)
    c: Coincident(g7,g4)
    c: Horizontal(g4)
    c: Horizontal(g6)
    c: Vertical(g5)
    c: Vertical(g7)
    c: Coincident(g4,g-6)
    c: PointOnObject(g5,g-4)
    c: Distance(g7) = 0.05
    c: Distance(g0) = 0.05
FEATURE [PartDesign::Pocket] Pocket164
  BaseFeature = -> Pad220
  Direction = (0,0,1)
  Length = 1.5
  Length2 = 5
  Profile = -> Sketch380
  ReferenceAxis = -> Sketch380 [N_Axis]
  Refine = true
  Suppressed = false
  Type = 0
FEATURE [Sketcher::SketchObject] Sketch381
  ArcFitTolerance = 1e-06
  AttachmentSupport = -> [Pocket164]
  ExternalGeometry = -> [Pocket164,Binder009]
  FullyConstrained = true
  MakeInternals = false
  MapMode = 5
  Placement = pos=(0,0,11.6) rot=(1,0,0;3.14159rad)
  sketch-geometry (4):
    g0: LineSegment StartX=-17.2 StartY=-9.1 StartZ=0 EndX=-19.6 EndY=-9.1 EndZ=0
    g1: LineSegment StartX=-19.6 StartY=-9.1 StartZ=0 EndX=-19.6 EndY=-14.5 EndZ=0
    g2: LineSegment StartX=-19.6 StartY=-14.5 StartZ=0 EndX=-17.2 EndY=-14.5 EndZ=0
    g3: LineSegment StartX=-17.2 StartY=-14.5 StartZ=0 EndX=-17.2 EndY=-9.1 EndZ=0
  constraints (12):
    c: Coincident(g0,g1)
    c: Coincident(g1,g2)
    c: Coincident(g2,g3)
    c: Coincident(g3,g0)
    c: Horizontal(g0)
    c: Horizontal(g2)
    c: Vertical(g1)
    c: Vertical(g3)
    c: PointOnObject(g0,g-5)
    c: PointOnObject(g0,g-4)
    c: DistanceX(g0,g0) = 2.4
    c: PointOnObject(g2,g-6)
FEATURE [PartDesign::Pad] Pad221
  BaseFeature = -> Pocket164
  Direction = (0,0,-1)
  Length = 1.5
  Length2 = 10
  Profile = -> Sketch381
  ReferenceAxis = -> Sketch381 [N_Axis]
  Refine = true
  Suppressed = false
  Type = 0
FEATURE [Sketcher::SketchObject] Sketch382
  ArcFitTolerance = 1e-06
  AttachmentSupport = -> [Pad221]
  ExternalGeometry = -> [Pad221]
  FullyConstrained = true
  MakeInternals = false
  MapMode = 5
  Placement = pos=(0,0,10.1) rot=(1,0,0;3.14159rad)
  sketch-geometry (8):
    g0: LineSegment StartX=-17.2 StartY=-9.1 StartZ=0 EndX=-19.6 EndY=-9.1 EndZ=0
    g1: LineSegment StartX=-19.6 StartY=-9.1 StartZ=0 EndX=-19.6 EndY=-9.15 EndZ=0
    g2: LineSegment StartX=-19.6 StartY=-9.15 StartZ=0 EndX=-17.2 EndY=-9.15 EndZ=0
    g3: LineSegment StartX=-17.2 StartY=-9.15 StartZ=0 EndX=-17.2 EndY=-9.1 EndZ=0
    g4: LineSegment StartX=-19.6 StartY=-14.5 StartZ=0 EndX=-17.2 EndY=-14.5 EndZ=0
    g5: LineSegment StartX=-17.2 StartY=-14.5 StartZ=0 EndX=-17.2 EndY=-14.45 EndZ=0
    g6: LineSegment StartX=-17.2 StartY=-14.45 StartZ=0 EndX=-19.6 EndY=-14.45 EndZ=0
    g7: LineSegment StartX=-19.6 StartY=-14.45 StartZ=0 EndX=-19.6 EndY=-14.5 EndZ=0
  constraints (22):
    c: Coincident(g0,g1)
    c: Coincident(g1,g2)
    c: Coincident(g2,g3)
    c: Coincident(g3,g0)
    c: Horizontal(g0)
    c: Horizontal(g2)
    c: Vertical(g1)
    c: Vertical(g3)
    c: Coincident(g0,g-3)
    c: PointOnObject(g1,g-6)
    c: DistanceY(g3,g3) = 0.05
    c: Coincident(g4,g5)
    c: Coincident(g5,g6)
    c: Coincident(g6,g7)
    c: Coincident(g7,g4)
    c: Horizontal(g4)
    c: Horizontal(g6)
    c: Vertical(g5)
    c: Vertical(g7)
    c: Coincident(g4,g-6)
    c: PointOnObject(g5,g-5)
    c: DistanceY(g5,g5) = 0.05
FEATURE [PartDesign::Pocket] Pocket165
  BaseFeature = -> Pad221
  Direction = (0,0,1)
  Length = 1.5
  Length2 = 5
  Profile = -> Sketch382
  ReferenceAxis = -> Sketch382 [N_Axis]
  Refine = true
  Suppressed = false
  Type = 0
FEATURE [Sketcher::SketchObject] Sketch383
  ArcFitTolerance = 1e-06
  AttachmentSupport = -> [Pocket165]
  ExternalGeometry = -> [Pocket165]
  FullyConstrained = true
  MakeInternals = false
  MapMode = 5
  Placement = pos=(0,14.45,0) rot=(0,0.707107,0.707107;3.14159rad)
  sketch-geometry (3):
    g0: LineSegment StartX=19.6 StartY=11.6 StartZ=0 EndX=19.6 EndY=10.1 EndZ=0
    g1: LineSegment StartX=19.6 StartY=11.6 StartZ=0 EndX=18.1 EndY=10.1 EndZ=0
    g2: LineSegment StartX=18.1 StartY=10.1 StartZ=0 EndX=19.6 EndY=10.1 EndZ=0
  constraints (7):
    c: Coincident(g0,g-3)
    c: Coincident(g0,g-4)
    c: Coincident(g1,g0)
    c: PointOnObject(g1,g-4)
    c: Coincident(g2,g1)
    c: Coincident(g2,g0)
    c: Angle(g1,g0) = 0.785398
FEATURE [PartDesign::Pocket] Pocket166
  BaseFeature = -> Pocket165
  Direction = (0,-1,2e-16)
  Length = 6
  Length2 = 5
  Profile = -> Sketch383
  ReferenceAxis = -> Sketch383 [N_Axis]
  Refine = true
  Suppressed = false
  Type = 0
FEATURE [Sketcher::SketchObject] Sketch384
  ArcFitTolerance = 1e-06
  AttachmentSupport = -> [Pocket166]
  ExternalGeometry = -> [Pocket166]
  FullyConstrained = true
  MakeInternals = false
  MapMode = 5
  Placement = pos=(0,5.2,0) rot=(1,0,0;1.5708rad)
  sketch-geometry (4):
    g0: LineSegment StartX=-14.4 StartY=11.6 StartZ=0 EndX=-14.4 EndY=13.5 EndZ=0
    g1: LineSegment StartX=-14.4 StartY=13.5 StartZ=0 EndX=-16.6 EndY=13.5 EndZ=0
    g2: LineSegment StartX=-16.6 StartY=13.5 StartZ=0 EndX=-16.6 EndY=11.6 EndZ=0
    g3: LineSegment StartX=-16.6 StartY=11.6 StartZ=0 EndX=-14.4 EndY=11.6 EndZ=0
  constraints (12):
    c: Coincident(g0,g1)
    c: Coincident(g1,g2)
    c: Coincident(g2,g3)
    c: Coincident(g3,g0)
    c: Vertical(g0)
    c: Vertical(g2)
    c: Horizontal(g1)
    c: Horizontal(g3)
    c: PointOnObject(g0,g-3)
    c: DistanceY(g0,g0) = 1.9
    c: DistanceX(g-3,g0) = 2
    c: DistanceX(g2,g-3) = 0.2
FEATURE [PartDesign::Pocket] Pocket167
  BaseFeature = -> Pocket166
  Direction = (0,1,-2e-16)
  Length = 5
  Length2 = 5
  Profile = -> Sketch384
  ReferenceAxis = -> Sketch384 [N_Axis]
  Refine = true
  Suppressed = false
  Type = 0
FEATURE [Sketcher::SketchObject] Sketch385
  ArcFitTolerance = 1e-06
  AttachmentSupport = -> [Pocket167]
  ExternalGeometry = -> [Pocket167]
  FullyConstrained = true
  MakeInternals = false
  MapMode = 5
  Placement = pos=(0,0,16.9) rot=(0,0,1;0rad)
  sketch-geometry (8):
    g0: LineSegment StartX=-16.4 StartY=6.7 StartZ=0 EndX=-15.2 EndY=6.7 EndZ=0
    g1: LineSegment StartX=-16.4 StartY=6.7 StartZ=0 EndX=-16.4 EndY=5.2 EndZ=0
    g2: LineSegment StartX=-16.4 StartY=5.2 StartZ=0 EndX=-6.1 EndY=5.2 EndZ=0
    g3: LineSegment StartX=-6.1 StartY=5.2 StartZ=0 EndX=-6.1 EndY=6.7 EndZ=0
    g4: LineSegment StartX=-6.1 StartY=6.7 StartZ=0 EndX=-7.3 EndY=6.7 EndZ=0
    g5: LineSegment StartX=-7.3 StartY=6.7 StartZ=0 EndX=-7.3 EndY=6.4 EndZ=0
    g6: LineSegment StartX=-7.3 StartY=6.4 StartZ=0 EndX=-15.2 EndY=6.4 EndZ=0
    g7: LineSegment StartX=-15.2 StartY=6.4 StartZ=0 EndX=-15.2 EndY=6.7 EndZ=0
  constraints (18):
    c: Coincident(g0,g-6)
    c: PointOnObject(g0,g-7)
    c: Horizontal(g0)
    c: Coincident(g1,g0)
    c: Coincident(g1,g-6)
    c: Coincident(g2,g1)
    c: Coincident(g2,g-5)
    c: Coincident(g3,g2)
    c: Coincident(g3,g-4)
    c: Coincident(g4,g3)
    c: Horizontal(g4)
    c: PointOnObject(g4,g-8)
    c: Coincident(g5,g4)
    c: Coincident(g5,g-8)
    c: Coincident(g6,g5)
    c: Coincident(g6,g-7)
    c: Coincident(g7,g6)
    c: Coincident(g7,g0)
FEATURE [PartDesign::Pad] Pad222
  BaseFeature = -> Pocket167
  Direction = (0,0,1)
  Length = 1
  Length2 = 10
  Profile = -> Sketch385
  ReferenceAxis = -> Sketch385 [N_Axis]
  Refine = true
  Suppressed = false
  Type = 0
FEATURE [PartDesign::Fillet] Fillet024
  Base = -> Pad222 [Edge113,Edge114]
  BaseFeature = -> Pad222
  Radius = 0.5
  Refine = true
  SupportTransform = false
  Suppressed = false
  UseAllEdges = false
FEATURE [Sketcher::SketchObject] Sketch386
  ArcFitTolerance = 1e-06
  AttachmentSupport = -> [Fillet024]
  ExternalGeometry = -> [Fillet024,Binder009]
  FullyConstrained = true
  MakeInternals = false
  MapMode = 5
  Placement = pos=(0,6.7,0) rot=(1,0,0;1.5708rad)
  sketch-geometry (4):
    g0: LineSegment StartX=-1.8 StartY=16.9 StartZ=0 EndX=-18.7 EndY=16.9 EndZ=0
    g1: LineSegment StartX=-18.7 StartY=16.9 StartZ=0 EndX=-18.7 EndY=25.6 EndZ=0
    g2: LineSegment StartX=-18.7 StartY=25.6 StartZ=0 EndX=0.2 EndY=25.6 EndZ=0
    g3: LineSegment StartX=0.2 StartY=25.6 StartZ=0 EndX=-1.8 EndY=16.9 EndZ=0
  constraints (13):
    c: PointOnObject(g0,g-3)
    c: Coincident(g0,g-6)
    c: Coincident(g1,g0)
    c: Vertical(g1)
    c: Coincident(g2,g1)
    c: Horizontal(g2)
    c: Coincident(g3,g2)
    c: Coincident(g3,g0)
    c: DistanceX(g0,g-5) = 2
    c: DistanceY(g-7,g-7) = 0
    c: DistanceY(g-7,g-7) = 0
    c: DistanceY(g-7,g1) = 14
    c: DistanceX(g-5,g2) = 0
FEATURE [PartDesign::Pad] Pad223
  BaseFeature = -> Fillet024
  Direction = (0,-1,2e-16)
  Length = 10.8
  Length2 = 10
  Profile = -> Sketch386
  ReferenceAxis = -> Sketch386 [N_Axis]
  Refine = true
  Reversed = true
  Suppressed = false
  Type = 0
FEATURE [PartDesign::Fillet] Fillet025
  Base = -> Pad223 [Edge93,Edge90,Edge96,Edge97,Edge95,Edge131,Edge94,Edge132]
  BaseFeature = -> Pad223
  Radius = 0.5
  Refine = true
  SupportTransform = false
  Suppressed = false
  UseAllEdges = false
FEATURE [Sketcher::SketchObject] Sketch387
  ArcFitTolerance = 1e-06
  AttachmentSupport = -> [Fillet025]
  ExternalGeometry = -> [Fillet025]
  FullyConstrained = true
  MakeInternals = false
  MapMode = 5
  Placement = pos=(3.5e-15,3.7e-15,16.9) rot=(1,0,0;3.14159rad)
  sketch-geometry (4):
    g0: LineSegment StartX=-1.3 StartY=-8.2 StartZ=0 EndX=-3.3 EndY=-8.2 EndZ=0
    g1: LineSegment StartX=-3.3 StartY=-8.2 StartZ=0 EndX=-3.3 EndY=-16 EndZ=0
    g2: LineSegment StartX=-3.3 StartY=-16 StartZ=0 EndX=-1.3 EndY=-16 EndZ=0
    g3: LineSegment StartX=-1.3 StartY=-16 StartZ=0 EndX=-1.3 EndY=-8.2 EndZ=0
  constraints (11):
    c: Coincident(g0,g1)
    c: Coincident(g1,g2)
    c: Coincident(g2,g3)
    c: Coincident(g3,g0)
    c: Horizontal(g0)
    c: Horizontal(g2)
    c: Vertical(g1)
    c: Vertical(g3)
    c: Coincident(g0,g-6)
    c: PointOnObject(g1,g-5)
    c: DistanceX(g2,g2) = 2
FEATURE [PartDesign::Pad] Pad224
  BaseFeature = -> Fillet025
  Direction = (0,0,-1)
  Length = 1.3
  Length2 = 10
  Profile = -> Sketch387
  ReferenceAxis = -> Sketch387 [N_Axis]
  Refine = true
  Suppressed = false
  Type = 0
FEATURE [Sketcher::SketchObject] Sketch388
  ArcFitTolerance = 1e-06
  AttachmentSupport = -> [Pad224]
  ExternalGeometry = -> [Pad224]
  FullyConstrained = true
  MakeInternals = false
  MapMode = 5
  Placement = pos=(0.2,0,0) rot=(0.57735,0.57735,0.57735;2.0944rad)
  sketch-geometry (4):
    g0: LineSegment StartX=8.2 StartY=24.1 StartZ=0 EndX=8.2 EndY=17.9 EndZ=0
    g1: LineSegment StartX=8.2 StartY=17.9 StartZ=0 EndX=16 EndY=17.9 EndZ=0
    g2: LineSegment StartX=16 StartY=17.9 StartZ=0 EndX=16 EndY=24.1 EndZ=0
    g3: LineSegment StartX=16 StartY=24.1 StartZ=0 EndX=8.2 EndY=24.1 EndZ=0
  constraints (13):
    c: Coincident(g0,g1)
    c: Coincident(g1,g2)
    c: Coincident(g2,g3)
    c: Coincident(g3,g0)
    c: Vertical(g0)
    c: Vertical(g2)
    c: Horizontal(g1)
    c: Horizontal(g3)
    c: DistanceY(g0,g-3) = 1.5
    c: DistanceX(g-4,g0) = 1.5
    c: DistanceY(g2,g2) = 6.2
    c: DistanceX(g1,g-5) = 1.5
    c: DistanceY(g-6,g0) = 0
FEATURE [PartDesign::Pocket] Pocket168
  BaseFeature = -> Pad224
  Direction = (-1,0,0)
  Length = 17.4
  Length2 = 5
  Profile = -> Sketch388
  ReferenceAxis = -> Sketch388 [N_Axis]
  Refine = true
  Suppressed = false
  Type = 0
FEATURE [Sketcher::SketchObject] Sketch389
  ArcFitTolerance = 1e-06
  AttachmentSupport = -> [Pocket168]
  ExternalGeometry = -> [Pocket168]
  FullyConstrained = true
  MakeInternals = false
  MapMode = 5
  Placement = pos=(0,6.7,-2.6e-15) rot=(1,0,0;1.5708rad)
  sketch-geometry (4):
    g0: LineSegment StartX=-15.2 StartY=17.9 StartZ=0 EndX=-7.3 EndY=17.9 EndZ=0
    g1: LineSegment StartX=-7.3 StartY=17.9 StartZ=0 EndX=-7.3 EndY=23.2 EndZ=0
    g2: LineSegment StartX=-7.3 StartY=23.2 StartZ=0 EndX=-15.2 EndY=23.2 EndZ=0
    g3: LineSegment StartX=-15.2 StartY=23.2 StartZ=0 EndX=-15.2 EndY=17.9 EndZ=0
  constraints (10):
    c: Coincident(g0,g1)
    c: Coincident(g1,g2)
    c: Coincident(g2,g3)
    c: Coincident(g3,g0)
    c: Horizontal(g2)
    c: Vertical(g1)
    c: Vertical(g3)
    c: Coincident(g0,g-4)
    c: Coincident(g0,g-3)
    c: DistanceY(g1,g1) = 5.3
FEATURE [PartDesign::Pocket] Pocket169
  BaseFeature = -> Pocket168
  Direction = (0,1,-2e-16)
  Length = 11
  Length2 = 5
  Profile = -> Sketch389
  ReferenceAxis = -> Sketch389 [N_Axis]
  Refine = true
  Suppressed = false
  Type = 0
FEATURE [Sketcher::SketchObject] Sketch390
  ArcFitTolerance = 1e-06
  AttachmentSupport = -> [Pocket169]
  ExternalGeometry = -> [Pocket169]
  FullyConstrained = true
  MakeInternals = false
  MapMode = 5
  Placement = pos=(3.5e-15,3.7e-15,16.9) rot=(1,0,0;3.14159rad)
  sketch-geometry (8):
    g0: LineSegment StartX=-15.2 StartY=-6.7 StartZ=0 EndX=-15.2 EndY=-8.2 EndZ=0
    g1: LineSegment StartX=-15.2 StartY=-8.2 StartZ=0 EndX=-17.2 EndY=-8.2 EndZ=0
    g2: LineSegment StartX=-17.2 StartY=-8.2 StartZ=0 EndX=-17.2 EndY=-16 EndZ=0
    g3: LineSegment StartX=-17.2 StartY=-16 StartZ=0 EndX=-3.3 EndY=-16 EndZ=0
    g4: LineSegment StartX=-3.3 StartY=-16 StartZ=0 EndX=-3.3 EndY=-8.2 EndZ=0
    g5: LineSegment StartX=-3.3 StartY=-8.2 StartZ=0 EndX=-7.3 EndY=-8.2 EndZ=0
    g6: LineSegment StartX=-7.3 StartY=-8.2 StartZ=0 EndX=-7.3 EndY=-6.7 EndZ=0
    g7: LineSegment StartX=-7.3 StartY=-6.7 StartZ=0 EndX=-15.2 EndY=-6.7 EndZ=0
  constraints (16):
    c: Coincident(g0,g-3)
    c: Coincident(g0,g-4)
    c: Coincident(g1,g0)
    c: Coincident(g1,g-5)
    c: Coincident(g2,g1)
    c: Coincident(g2,g-9)
    c: Coincident(g3,g2)
    c: Coincident(g3,g-9)
    c: Coincident(g4,g3)
    c: Coincident(g4,g-8)
    c: Coincident(g5,g4)
    c: Coincident(g5,g-7)
    c: Coincident(g6,g5)
    c: Coincident(g6,g-7)
    c: Coincident(g7,g6)
    c: Coincident(g7,g0)
FEATURE [PartDesign::Pocket] Pocket170
  BaseFeature = -> Pocket169
  Direction = (0,0,1)
  Length = 2
  Length2 = 5
  Profile = -> Sketch390
  ReferenceAxis = -> Sketch390 [N_Axis]
  Refine = true
  Suppressed = false
  Type = 0
FEATURE [Sketcher::SketchObject] Sketch391
  ArcFitTolerance = 1e-06
  AttachmentSupport = -> [Pocket170]
  ExternalGeometry = -> [Pocket170]
  FullyConstrained = true
  MakeInternals = false
  MapMode = 5
  Placement = pos=(0,17.5,-8.9e-15) rot=(0,0.707107,0.707107;3.14159rad)
  sketch-geometry (4):
    g0: LineSegment StartX=5.3 StartY=23.1 StartZ=0 EndX=3.3 EndY=23.1 EndZ=0
    g1: LineSegment StartX=3.3 StartY=23.1 StartZ=0 EndX=3.3 EndY=17.9 EndZ=0
    g2: LineSegment StartX=3.3 StartY=17.9 StartZ=0 EndX=5.3 EndY=17.9 EndZ=0
    g3: LineSegment StartX=5.3 StartY=17.9 StartZ=0 EndX=5.3 EndY=23.1 EndZ=0
  constraints (12):
    c: Coincident(g0,g1)
    c: Coincident(g1,g2)
    c: Coincident(g2,g3)
    c: Coincident(g3,g0)
    c: Horizontal(g0)
    c: Horizontal(g2)
    c: Vertical(g1)
    c: Vertical(g3)
    c: DistanceX(g0,g0) = 2
    c: DistanceY(g3,g3) = 5.2
    c: DistanceY(g-3,g2) = 0
    c: DistanceX(g2,g-3) = 2
FEATURE [PartDesign::Pocket] Pocket171
  BaseFeature = -> Pocket170
  Direction = (0,-1,2e-16)
  Length = 5
  Length2 = 5
  Profile = -> Sketch391
  ReferenceAxis = -> Sketch391 [N_Axis]
  Refine = true
  Suppressed = false
  Type = 0
FEATURE [Sketcher::SketchObject] Sketch392
  ArcFitTolerance = 1e-06
  AttachmentSupport = -> [Pocket171]
  ExternalGeometry = -> [Pocket171]
  FullyConstrained = true
  MakeInternals = false
  MapMode = 5
  Placement = pos=(0,5.6e-15,25.6) rot=(0,0,1;0rad)
  sketch-geometry (1):
    g0: Circle CenterX=-9.25 CenterY=12.1 CenterZ=0 NormalX=0 NormalY=0 NormalZ=1 AngleXU=0 Radius=2.75
  constraints (5):
    c: Diameter(g0) = 5.5
    c: DistanceX(g-6,g-5) = 18.9
    c: DistanceX(g-6,g0) = 9.45
    c: DistanceY(g-4,g-3) = 10.8
    c: DistanceY(g-4,g0) = 5.4
FEATURE [PartDesign::Pocket] Pocket172
  BaseFeature = -> Pocket171
  Direction = (0,0,-1)
  Length = 5
  Length2 = 5
  Profile = -> Sketch392
  ReferenceAxis = -> Sketch392 [N_Axis]
  Refine = true
  Suppressed = false
  Type = 0
FEATURE [Sketcher::SketchObject] Sketch393
  ArcFitTolerance = 1e-06
  AttachmentSupport = -> [Pocket172]
  ExternalGeometry = -> [Pocket172]
  FullyConstrained = true
  MakeInternals = false
  MapMode = 5
  Placement = pos=(0,17.5,-8.9e-15) rot=(0,0.707107,0.707107;3.14159rad)
  sketch-geometry (12):
    g0: LineSegment StartX=6.05 StartY=24.45 StartZ=0 EndX=6.05 EndY=11.6 EndZ=0
    g1: LineSegment StartX=6.05 StartY=11.6 StartZ=0 EndX=16.45 EndY=11.6 EndZ=0
    g2: LineSegment StartX=16.45 StartY=11.6 StartZ=0 EndX=16.45 EndY=24.45 EndZ=0
    g3: LineSegment StartX=16.45 StartY=24.45 StartZ=0 EndX=6.05 EndY=24.45 EndZ=0
    g4: LineSegment StartX=6.55 StartY=23.95 StartZ=0 EndX=6.55 EndY=12.1 EndZ=0
    g5: LineSegment StartX=6.55 StartY=12.1 StartZ=0 EndX=15.95 EndY=12.1 EndZ=0
    g6: LineSegment StartX=15.95 StartY=12.1 StartZ=0 EndX=15.95 EndY=23.95 EndZ=0
    g7: LineSegment StartX=15.95 StartY=23.95 StartZ=0 EndX=6.55 EndY=23.95 EndZ=0
    g8: LineSegment StartX=7.3 StartY=17.15 StartZ=0 EndX=7.3 EndY=16.65 EndZ=0
    g9: LineSegment StartX=7.3 StartY=16.65 StartZ=0 EndX=8.8 EndY=16.65 EndZ=0
    g10: LineSegment StartX=8.8 StartY=16.65 StartZ=0 EndX=8.8 EndY=17.15 EndZ=0
    g11: LineSegment StartX=8.8 StartY=17.15 StartZ=0 EndX=7.3 EndY=17.15 EndZ=0
  constraints (36):
    c: Coincident(g0,g1)
    c: Coincident(g1,g2)
    c: Coincident(g2,g3)
    c: Coincident(g3,g0)
    c: Vertical(g0)
    c: Vertical(g2)
    c: Horizontal(g1)
    c: Horizontal(g3)
    c: PointOnObject(g1,g-3)
    c: Coincident(g4,g5)
    c: Coincident(g5,g6)
    c: Coincident(g6,g7)
    c: Coincident(g7,g4)
    c: Vertical(g4)
    c: Vertical(g6)
    c: Horizontal(g5)
    c: Horizontal(g7)
    c: Coincident(g8,g9)
    c: Coincident(g9,g10)
    c: Coincident(g10,g11)
    c: Coincident(g11,g8)
    c: Vertical(g8)
    c: Vertical(g10)
    c: Horizontal(g9)
    c: Horizontal(g11)
    c: DistanceX(g0,g4) = 0.5
    c: DistanceX(g5,g1) = 0.5
    c: DistanceY(g10,g10) = 0.5
    c: DistanceY(g0,g4) = 0.5
    c: DistanceY(g4,g0) = 0.5
    c: DistanceX(g4,g-4) = 0.75
    c: DistanceX(g-4,g6) = 0.75
    c: DistanceY(g-4,g4) = 0.75
    c: DistanceX(g-5,g8) = 0
    c: DistanceY(g8,g-5) = 0.75
    c: DistanceX(g9,g9) = 1.5
FEATURE [PartDesign::Pad] Pad225
  BaseFeature = -> Pocket172
  Direction = (0,1,-2e-16)
  Length = 0.5
  Length2 = 10
  Profile = -> Sketch393
  ReferenceAxis = -> Sketch393 [N_Axis]
  Refine = true
  Suppressed = false
  Type = 0
FEATURE [PartDesign::Pocket] Pocket173
  BaseFeature = -> Pad225
  Direction = (0,2e-16,1)
  Length = 0.3
  Length2 = 5
  Profile = -> Pad225 [Face25]
  Refine = true
  Suppressed = false
  Type = 0
FEATURE [Sketcher::SketchObject] Sketch394
  ArcFitTolerance = 1e-06
  AttachmentSupport = -> [Pocket173]
  ExternalGeometry = -> [Pocket173]
  FullyConstrained = true
  MakeInternals = false
  MapMode = 5
  Placement = pos=(0,6.7,-2.6e-15) rot=(1,0,0;1.5708rad)
  sketch-geometry (4):
    g0: LineSegment StartX=-16.6 StartY=11.6 StartZ=0 EndX=-16.6 EndY=13.6 EndZ=0
    g1: LineSegment StartX=-16.6 StartY=13.6 StartZ=0 EndX=-18.2 EndY=13.6 EndZ=0
    g2: LineSegment StartX=-18.2 StartY=13.6 StartZ=0 EndX=-18.2 EndY=11.6 EndZ=0
    g3: LineSegment StartX=-18.2 StartY=11.6 StartZ=0 EndX=-16.6 EndY=11.6 EndZ=0
  constraints (11):
    c: Coincident(g0,g1)
    c: Coincident(g1,g2)
    c: Coincident(g2,g3)
    c: Coincident(g3,g0)
    c: Vertical(g0)
    c: Vertical(g2)
    c: Horizontal(g1)
    c: Horizontal(g3)
    c: Coincident(g0,g-4)
    c: PointOnObject(g1,g-5)
    c: DistanceY(g2,g2) = 2
FEATURE [PartDesign::Pad] Pad226
  BaseFeature = -> Pocket173
  Direction = (0,-1,2e-16)
  Length = 1.5
  Length2 = 10
  Profile = -> Sketch394
  ReferenceAxis = -> Sketch394 [N_Axis]
  Refine = true
  Suppressed = false
  Type = 0
FEATURE [Sketcher::SketchObject] Sketch397
  ArcFitTolerance = 1e-06
  AttachmentSupport = -> [Pad226]
  ExternalGeometry = -> [Pad226]
  FullyConstrained = true
  MakeInternals = false
  MapMode = 5
  Placement = pos=(0,0,10.1) rot=(1,0,0;3.14159rad)
  sketch-geometry (4):
    g0: LineSegment StartX=-1.3 StartY=-9.75 StartZ=0 EndX=-1.3 EndY=-14.45 EndZ=0
    g1: LineSegment StartX=-1.3 StartY=-14.45 StartZ=0 EndX=2 EndY=-14.45 EndZ=0
    g2: LineSegment StartX=2 StartY=-14.45 StartZ=0 EndX=2 EndY=-9.75 EndZ=0
    g3: LineSegment StartX=2 StartY=-9.75 StartZ=0 EndX=-1.3 EndY=-9.75 EndZ=0
  constraints (10):
    c: Coincident(g0,g1)
    c: Coincident(g1,g2)
    c: Coincident(g2,g3)
    c: Coincident(g3,g0)
    c: Vertical(g0)
    c: Vertical(g2)
    c: Horizontal(g1)
    c: Horizontal(g3)
    c: Coincident(g0,g-6)
    c: Coincident(g1,g-5)
FEATURE [PartDesign::Pad] Pad228
  BaseFeature = -> Pad226
  Direction = (0,0,-1)
  Length = 0.1
  Length2 = 10
  Profile = -> Sketch397
  ReferenceAxis = -> Sketch397 [N_Axis]
  Refine = true
  Suppressed = false
  Type = 0
FEATURE [Sketcher::SketchObject] Sketch398
  ArcFitTolerance = 1e-06
  AttachmentSupport = -> [Pad228]
  ExternalGeometry = -> [Pad228]
  FullyConstrained = true
  MakeInternals = false
  MapMode = 5
  Placement = pos=(0,0,11.6) rot=(0,0,1;0rad)
  sketch-geometry (4):
    g0: LineSegment StartX=0.2 StartY=14.45 StartZ=0 EndX=0.2 EndY=9.75 EndZ=0
    g1: LineSegment StartX=0.2 StartY=9.75 StartZ=0 EndX=2 EndY=9.75 EndZ=0
    g2: LineSegment StartX=2 StartY=9.75 StartZ=0 EndX=2 EndY=14.45 EndZ=0
    g3: LineSegment StartX=2 StartY=14.45 StartZ=0 EndX=0.2 EndY=14.45 EndZ=0
  constraints (10):
    c: Coincident(g0,g1)
    c: Coincident(g1,g2)
    c: Coincident(g2,g3)
    c: Coincident(g3,g0)
    c: Vertical(g0)
    c: Vertical(g2)
    c: Horizontal(g1)
    c: Horizontal(g3)
    c: Coincident(g1,g-5)
    c: Coincident(g-6,g0)
FEATURE [PartDesign::Pocket] Pocket175
  BaseFeature = -> Pad228
  Direction = (0,0,-1)
  Length = 0.1
  Length2 = 5
  Profile = -> Sketch398
  ReferenceAxis = -> Sketch398 [N_Axis]
  Refine = true
  Suppressed = false
  Type = 0
FEATURE [PartDesign::Body] Body020  label="Cab"
  AllowCompound = false
  Group = -> [Binder009,Sketch378,Pad219,Sketch379,Pad220,Sketch380,Pocket164,Sketch381,Pad221,Sketch382,Pocket165,Sketch383,Pocket166,Sketch384,Pocket167,Sketch385,Pad222,Fillet024,Sketch386,Pad223,Fillet025,Sketch387,Pad224,Sketch388,Pocket168,Sketch389,Pocket169,Sketch390,Pocket170,Sketch391,Pocket171,Sketch392,Pocket172,Sketch393,Pad225,Pocket173,Sketch394,Pad226,Sketch397,Pad228,Sketch398,Pocket175,+13 more]
  Origin = -> Origin021
  Tip = -> Pad250
COMPONENT P11 — recipe-attached ("Roof_Clip", modeled in this document).
Construction recipe (the document's own serialized feature program — sketch geometry with constraints, then the solid features built on it; lengths are millimeters unless a unit is written):

FEATURE [PartDesign::SubShapeBinder] Binder010
  BindCopyOnChange = 0
  BindMode = 2
  ClaimChildren = false
  Context = -> Body022 [Binder010.]
  Fuse = false
  MakeFace = true
  OffsetFill = false
  OffsetIntersection = false
  OffsetJoinType = 0
  OffsetOpenResult = false
  PartialLoad = false
  Refine = true
  Relative = true
  _Version = 2
FEATURE [Sketcher::SketchObject] Sketch427
  ArcFitTolerance = 1e-06
  AttachmentSupport = -> [Binder010]
  ExternalGeometry = -> [Binder010]
  FullyConstrained = true
  MakeInternals = false
  MapMode = 5
  Placement = pos=(0,0,11.6) rot=(0,0,1;0rad)
  sketch-geometry (4):
    g0: LineSegment StartX=-25.3 StartY=-13.2 StartZ=0 EndX=-25.3 EndY=-16 EndZ=0
    g1: LineSegment StartX=-25.3 StartY=-16 StartZ=0 EndX=-23.3 EndY=-16 EndZ=0
    g2: LineSegment StartX=-23.3 StartY=-16 StartZ=0 EndX=-23.3 EndY=-13.2 EndZ=0
    g3: LineSegment StartX=-23.3 StartY=-13.2 StartZ=0 EndX=-25.3 EndY=-13.2 EndZ=0
  constraints (10):
    c: Coincident(g0,g1)
    c: Coincident(g1,g2)
    c: Coincident(g2,g3)
    c: Coincident(g3,g0)
    c: Vertical(g0)
    c: Vertical(g2)
    c: Horizontal(g1)
    c: Horizontal(g3)
    c: Coincident(g0,g-4)
    c: Coincident(g1,g-6)
FEATURE [PartDesign::Pad] Pad245
  Direction = (0,0,1)
  Length = 2.95
  Length2 = 10
  Profile = -> Sketch427
  ReferenceAxis = -> Sketch427 [N_Axis]
  Refine = true
  Suppressed = false
  Type = 0
FEATURE [Sketcher::SketchObject] Sketch428
  ArcFitTolerance = 1e-06
  AttachmentSupport = -> [Pad245]
  ExternalGeometry = -> [Pad245]
  FullyConstrained = true
  MakeInternals = false
  MapMode = 5
  Placement = pos=(0,-16,0) rot=(1,0,0;1.5708rad)
  sketch-geometry (8):
    g0: LineSegment StartX=-28.4 StartY=11.6 StartZ=0 EndX=-28.4 EndY=14.55 EndZ=0
    g1: LineSegment StartX=-30.4 StartY=14.55 StartZ=0 EndX=-30.4 EndY=11.6 EndZ=0
    g2: LineSegment StartX=-30.4 StartY=11.6 StartZ=0 EndX=-28.4 EndY=11.6 EndZ=0
    g3: LineSegment [constr] StartX=-28.4 StartY=14.55 StartZ=0 EndX=-25.3 EndY=14.55 EndZ=0
    g4: LineSegment [constr] StartX=-25.3 StartY=11.6 StartZ=0 EndX=-28.4 EndY=11.6 EndZ=0
    g5: ArcOfCircle CenterX=-26.85 CenterY=14.55 CenterZ=0 NormalX=0 NormalY=0 NormalZ=1 AngleXU=0 Radius=1.55 StartAngle=-8e-15 EndAngle=3.14159
    g6: ArcOfCircle CenterX=-26.85 CenterY=14.55 CenterZ=0 NormalX=0 NormalY=0 NormalZ=1 AngleXU=0 Radius=3.55 StartAngle=-3.6e-15 EndAngle=3.14159
    g7: LineSegment StartX=-25.3 StartY=14.55 StartZ=0 EndX=-23.3 EndY=14.55 EndZ=0
  constraints (21):
    c: Coincident(g1,g2)
    c: Coincident(g2,g0)
    c: Vertical(g0)
    c: Vertical(g1)
    c: Horizontal(g2)
    c: Coincident(g3,g0)
    c: Coincident(g3,g-3)
    c: Horizontal(g3)
    c: DistanceX(g3,g3) = 3.1
    c: DistanceX(g1,g0) = 2
    c: Coincident(g4,g-3)
    c: Coincident(g4,g0)
    c: Horizontal(g4)
    c: Coincident(g5,g0)
    c: Coincident(g5,g3)
    c: Coincident(g6,g1)
    c: Coincident(g6,g-4)
    c: PointOnObject(g5,g3)
    c: Coincident(g6,g5)
    c: Coincident(g7,g3)
    c: Coincident(g7,g6)
FEATURE [PartDesign::Pad] Pad246
  BaseFeature = -> Pad245
  Direction = (0,-1,2e-16)
  Length = 2.8
  Length2 = 10
  Profile = -> Sketch428
  ReferenceAxis = -> Sketch428 [N_Axis]
  Refine = true
  Reversed = true
  Suppressed = false
  Type = 0
FEATURE [Sketcher::SketchObject] Sketch429
  ArcFitTolerance = 1e-06
  AttachmentSupport = -> [Pad246]
  ExternalGeometry = -> [Pad246]
  FullyConstrained = true
  MakeInternals = false
  MapMode = 5
  Placement = pos=(0,2.6e-15,11.6) rot=(1,0,0;3.14159rad)
  sketch-geometry (2):
    g0: Circle CenterX=-29.4 CenterY=14.6 CenterZ=0 NormalX=0 NormalY=0 NormalZ=1 AngleXU=0 Radius=0.55
    g1: Circle CenterX=-24.3 CenterY=14.6 CenterZ=0 NormalX=0 NormalY=0 NormalZ=1 AngleXU=0 Radius=0.55
  constraints (6):
    c: Radius(g0) = 0.55
    c: Radius(g1) = 0.55
    c: DistanceX(g-3,g0) = 1
    c: DistanceX(g1,g-4) = 1
    c: DistanceY(g0,g-3) = 1.4
    c: DistanceY(g1,g-4) = 1.4
FEATURE [PartDesign::Pad] Pad247
  BaseFeature = -> Pad246
  Direction = (0,0,-1)
  Length = 1.5
  Length2 = 10
  Profile = -> Sketch429
  ReferenceAxis = -> Sketch429 [N_Axis]
  Refine = true
  Suppressed = false
  Type = 0
FEATURE [PartDesign::Body] Body022  label="Roof_Clip"
  AllowCompound = false
  Group = -> [Binder010,Sketch427,Pad245,Sketch428,Pad246,Sketch429,Pad247]
  Origin = -> Origin023
  Tip = -> Pad247
COMPONENT P12 — recipe-attached ("Arm_Rod_Collar2", modeled in this document).
Construction recipe (the document's own serialized feature program — sketch geometry with constraints, then the solid features built on it; lengths are millimeters unless a unit is written):

FEATURE [Sketcher::SketchObject] Sketch435
  ArcFitTolerance = 1e-06
  AttachmentSupport = -> [XY_Plane025]
  FullyConstrained = true
  MakeInternals = false
  MapMode = 5
  sketch-geometry (2):
    g0: Circle CenterX=0 CenterY=0 CenterZ=0 NormalX=0 NormalY=0 NormalZ=1 AngleXU=0 Radius=0.8
    g1: Circle CenterX=0 CenterY=0 CenterZ=0 NormalX=0 NormalY=0 NormalZ=1 AngleXU=0 Radius=1.425
  constraints (4):
    c: Coincident(g0,g-1)
    c: Coincident(g1,g0)
    c: Diameter(g0) = 1.6
    c: Diameter(g1) = 2.85
FEATURE [PartDesign::Pad] Pad252
  Direction = (0,0,1)
  Length = 3.3
  Length2 = 10
  Profile = -> Sketch435
  ReferenceAxis = -> Sketch435 [N_Axis]
  Refine = true
  Suppressed = false
  Type = 0
FEATURE [PartDesign::Body] Body023  label="Arm_Rod_Collar2"
  AllowCompound = false
  Group = -> [Sketch435,Pad252]
  Origin = -> Origin025
  Placement = pos=(-15.5,14,7.6) rot=(1,0,0;1.5708rad)
  Tip = -> Pad252
COMPONENT P13 — recipe-attached ("Arm_Stop2", modeled in this document).
Construction recipe (the document's own serialized feature program — sketch geometry with constraints, then the solid features built on it; lengths are millimeters unless a unit is written):

FEATURE [Sketcher::SketchObject] Sketch415
  ArcFitTolerance = 1e-06
  AttachmentOffset = pos=(-18.5,6,-1.7) rot=(0,0,1;0rad)
  AttachmentSupport = -> [XZ_Plane022]
  FullyConstrained = true
  MakeInternals = false
  MapMode = 5
  Placement = pos=(-18.5,1.7,6) rot=(1,0,0;1.5708rad)
  sketch-geometry (5):
    g0: LineSegment StartX=0 StartY=0 StartZ=0 EndX=6 EndY=0 EndZ=0
    g1: LineSegment StartX=6 StartY=0 StartZ=0 EndX=6 EndY=5 EndZ=0
    g2: LineSegment StartX=6 StartY=5 StartZ=0 EndX=0 EndY=5 EndZ=0
    g3: LineSegment StartX=0 StartY=5 StartZ=0 EndX=0 EndY=0 EndZ=0
    g4: Circle CenterX=3 CenterY=2.5 CenterZ=0 NormalX=0 NormalY=0 NormalZ=1 AngleXU=0 Radius=0.7
  constraints (14):
    c: Coincident(g0,g1)
    c: Coincident(g1,g2)
    c: Coincident(g2,g3)
    c: Coincident(g3,g0)
    c: Horizontal(g0)
    c: Horizontal(g2)
    c: Vertical(g1)
    c: Vertical(g3)
    c: Coincident(g0,g-1)
    c: DistanceX(g2,g2) = 6
    c: DistanceY(g3,g3) = 5
    c: Diameter(g4) = 1.4
    c: DistanceX(g2,g4) = 3
    c: DistanceY(g4,g2) = 2.5
FEATURE [PartDesign::Pad] Pad242
  Direction = (0,-1,2e-16)
  Length = 0.5
  Length2 = 10
  Placement = pos=(0,0,0) rot=(1,0,0;1.5708rad)
  Profile = -> Sketch415
  ReferenceAxis = -> Sketch415 [N_Axis]
  Refine = true
  Suppressed = false
  Type = 0
FEATURE [Sketcher::SketchObject] Sketch416
  ArcFitTolerance = 1e-06
  AttachmentSupport = -> [Pad242]
  ExternalGeometry = -> [Pad242]
  FullyConstrained = true
  MakeInternals = false
  MapMode = 5
  Placement = pos=(0,1.2,0) rot=(1,0,0;1.5708rad)
  sketch-geometry (4):
    g0: LineSegment StartX=-14.9 StartY=8.86056 StartZ=0 EndX=-14.9 EndY=11 EndZ=0
    g1: LineSegment StartX=-14.9 StartY=11 StartZ=0 EndX=-16.1 EndY=11 EndZ=0
    g2: LineSegment StartX=-16.1 StartY=11 StartZ=0 EndX=-16.1 EndY=8.86056 EndZ=0
    g3: LineSegment StartX=-16.1 StartY=8.86056 StartZ=0 EndX=-14.9 EndY=8.86056 EndZ=0
  constraints (12):
    c: Coincident(g0,g1)
    c: Vertical(g0)
    c: Horizontal(g1)
    c: PointOnObject(g1,g-3)
    c: PointOnObject(g0,g-4)
    c: Coincident(g2,g1)
    c: PointOnObject(g2,g-4)
    c: Coincident(g3,g2)
    c: Coincident(g3,g0)
    c: Vertical(g2)
    c: Horizontal(g3)
    c: DistanceX(g-3,g1) = 2.4
FEATURE [PartDesign::Pocket] Pocket190
  BaseFeature = -> Pad242
  Direction = (0,1,-2e-16)
  Length = 5
  Length2 = 5
  Placement = pos=(0,0,0) rot=(1,0,0;1.5708rad)
  Profile = -> Sketch416
  ReferenceAxis = -> Sketch416 [N_Axis]
  Refine = true
  Suppressed = false
  Type = 0
FEATURE [PartDesign::Body] Body021  label="Arm_Stop1"
  AllowCompound = false
  Group = -> [Sketch415,Pad242,Sketch416,Pocket190]
  Origin = -> Origin022
  Placement = pos=(-31,0,16.1) rot=(0,1,0;3.14159rad)
  Tip = -> Pocket190
COMPONENT P14 — recipe-attached ("L_Fist", modeled in this document).
Construction recipe (the document's own serialized feature program — sketch geometry with constraints, then the solid features built on it; lengths are millimeters unless a unit is written):

FEATURE [Sketcher::SketchObject] Sketch250
  ArcFitTolerance = 1e-06
  AttachmentSupport = -> [XY_Plane008]
  FullyConstrained = true
  MakeInternals = false
  MapMode = 5
  sketch-geometry (10):
    g0: ArcOfCircle CenterX=0 CenterY=0 CenterZ=0 NormalX=0 NormalY=0 NormalZ=1 AngleXU=0 Radius=1.95 StartAngle=1.5708 EndAngle=4.71239
    g1: LineSegment StartX=0 StartY=-1.95 StartZ=0 EndX=4.5 EndY=-1.95 EndZ=0
    g2: LineSegment StartX=4.5 StartY=-1.95 StartZ=0 EndX=4.5 EndY=-4 EndZ=0
    g3: LineSegment StartX=4.5 StartY=-4 StartZ=0 EndX=9.1 EndY=-4 EndZ=0
    g4: LineSegment StartX=9.1 StartY=-4 StartZ=0 EndX=11.5 EndY=-1.6 EndZ=0
    g5: LineSegment StartX=11.5 StartY=-1.6 StartZ=0 EndX=11.5 EndY=1.6 EndZ=0
    g6: LineSegment StartX=11.5 StartY=1.6 StartZ=0 EndX=9.1 EndY=4 EndZ=0
    g7: LineSegment StartX=9.1 StartY=4 StartZ=0 EndX=4.5 EndY=4 EndZ=0
    g8: LineSegment StartX=4.5 StartY=4 StartZ=0 EndX=4.5 EndY=1.95 EndZ=0
    g9: LineSegment StartX=4.5 StartY=1.95 StartZ=0 EndX=0 EndY=1.95 EndZ=0
  constraints (30):
    c: PointOnObject(g0,g-2)
    c: PointOnObject(g0,g-2)
    c: Coincident(g1,g0)
    c: Horizontal(g1)
    c: Coincident(g2,g1)
    c: Vertical(g2)
    c: Coincident(g3,g2)
    c: Horizontal(g3)
    c: Coincident(g4,g3)
    c: Coincident(g5,g4)
    c: Vertical(g5)
    c: Coincident(g6,g5)
    c: Coincident(g7,g6)
    c: Horizontal(g7)
    c: Coincident(g8,g7)
    c: Vertical(g8)
    c: Coincident(g9,g8)
    c: Coincident(g9,g0)
    c: Horizontal(g9)
    c: Coincident(g-1,g0)
    c: Diameter(g0) = 3.9
    c: DistanceY(g2,g7) = 8
    c: DistanceY(g8,g7) = 2.05
    c: DistanceX(g8,g5) = 7
    c: DistanceX(g0,g8) = 4.5
    c: DistanceX(g0,g1) = 4.5
    c: DistanceY(g4,g5) = 3.2
    c: DistanceY(g0,g5) = 1.6
    c: Angle(g6,g5) = 2.35619
    c: Angle(g5,g4) = 2.35619
FEATURE [PartDesign::Pad] Pad151
  Direction = (0,0,1)
  Length = 2.25
  Length2 = 10
  Profile = -> Sketch250
  ReferenceAxis = -> Sketch250 [N_Axis]
  Refine = true
  Suppressed = false
  Type = 0
FEATURE [Sketcher::SketchObject] Sketch251
  ArcFitTolerance = 1e-06
  AttachmentSupport = -> [Pad151]
  FullyConstrained = true
  MakeInternals = false
  MapMode = 5
  Placement = pos=(0,0,2.25) rot=(0,0,1;0rad)
  sketch-geometry (1):
    g0: Circle CenterX=0 CenterY=0 CenterZ=0 NormalX=0 NormalY=0 NormalZ=1 AngleXU=0 Radius=1
  constraints (2):
    c: Coincident(g0,g-1)
    c: Diameter(g0) = 2
FEATURE [PartDesign::Pad] Pad152
  BaseFeature = -> Pad151
  Direction = (0,0,1)
  Length = 1.3
  Length2 = 10
  Profile = -> Sketch251
  ReferenceAxis = -> Sketch251 [N_Axis]
  Refine = true
  Suppressed = false
  Type = 0
FEATURE [Sketcher::SketchObject] Sketch252
  ArcFitTolerance = 1e-06
  AttachmentSupport = -> [Pad152]
  FullyConstrained = true
  MakeInternals = false
  MapMode = 5
  Placement = pos=(0,0,0) rot=(1,0,0;3.14159rad)
  sketch-geometry (1):
    g0: Circle CenterX=0 CenterY=0 CenterZ=0 NormalX=0 NormalY=0 NormalZ=1 AngleXU=0 Radius=1
  constraints (2):
    c: Coincident(g0,g-1)
    c: Diameter(g0) = 2
FEATURE [PartDesign::Pad] Pad153
  BaseFeature = -> Pad152
  Direction = (0,0,-1)
  Length = 1.3
  Length2 = 10
  Profile = -> Sketch252
  ReferenceAxis = -> Sketch252 [N_Axis]
  Refine = true
  Suppressed = false
  Type = 0
FEATURE [Sketcher::SketchObject] Sketch253
  ArcFitTolerance = 1e-06
  AttachmentSupport = -> [Pad153]
  ExternalGeometry = -> [Pad153]
  FullyConstrained = true
  MakeInternals = false
  MapMode = 5
  Placement = pos=(0,0,0) rot=(1,0,0;3.14159rad)
  sketch-geometry (6):
    g0: LineSegment StartX=4.5 StartY=4 StartZ=0 EndX=9.1 EndY=4 EndZ=0
    g1: LineSegment StartX=9.1 StartY=4 StartZ=0 EndX=11.5 EndY=1.6 EndZ=0
    g2: LineSegment StartX=11.5 StartY=1.6 StartZ=0 EndX=11.5 EndY=-1.6 EndZ=0
    g3: LineSegment StartX=11.5 StartY=-1.6 StartZ=0 EndX=9.1 EndY=-4 EndZ=0
    g4: LineSegment StartX=9.1 StartY=-4 StartZ=0 EndX=4.5 EndY=-4 EndZ=0
    g5: LineSegment StartX=4.5 StartY=-4 StartZ=0 EndX=4.5 EndY=4 EndZ=0
  constraints (12):
    c: Coincident(g0,g-3)
    c: Coincident(g0,g-4)
    c: Coincident(g1,g0)
    c: Coincident(g1,g-5)
    c: Coincident(g2,g1)
    c: Coincident(g2,g-6)
    c: Coincident(g3,g2)
    c: Coincident(g3,g-7)
    c: Coincident(g4,g3)
    c: Coincident(g4,g-7)
    c: Coincident(g5,g4)
    c: Coincident(g5,g0)
FEATURE [PartDesign::Pocket] Pocket103
  BaseFeature = -> Pad153
  Direction = (0,0,1)
  Length = 1.25
  Length2 = 5
  Profile = -> Sketch253
  ReferenceAxis = -> Sketch253 [N_Axis]
  Refine = true
  Suppressed = false
  Type = 0
FEATURE [Sketcher::SketchObject] Sketch254
  ArcFitTolerance = 1e-06
  AttachmentSupport = -> [Pocket103]
  ExternalGeometry = -> [Pocket103]
  FullyConstrained = true
  MakeInternals = false
  MapMode = 5
  Placement = pos=(0,0,2.25) rot=(0,0,1;0rad)
  sketch-geometry (6):
    g0: LineSegment StartX=4.5 StartY=4 StartZ=0 EndX=9.1 EndY=4 EndZ=0
    g1: LineSegment StartX=9.1 StartY=4 StartZ=0 EndX=11.5 EndY=1.6 EndZ=0
    g2: LineSegment StartX=11.5 StartY=1.6 StartZ=0 EndX=11.5 EndY=-1.6 EndZ=0
    g3: LineSegment StartX=11.5 StartY=-1.6 StartZ=0 EndX=9.1 EndY=-4 EndZ=0
    g4: LineSegment StartX=9.1 StartY=-4 StartZ=0 EndX=4.5 EndY=-4 EndZ=0
    g5: LineSegment StartX=4.5 StartY=-4 StartZ=0 EndX=4.5 EndY=4 EndZ=0
  constraints (12):
    c: Coincident(g0,g-3)
    c: Coincident(g0,g-4)
    c: Coincident(g1,g0)
    c: Coincident(g1,g-5)
    c: Coincident(g2,g1)
    c: Coincident(g2,g-6)
    c: Coincident(g3,g2)
    c: Coincident(g3,g-7)
    c: Coincident(g4,g3)
    c: Coincident(g4,g-7)
    c: Coincident(g5,g4)
    c: Coincident(g5,g0)
FEATURE [PartDesign::Pad] Pad154
  BaseFeature = -> Pocket103
  Direction = (0,0,1)
  Length = 1
  Length2 = 10
  Profile = -> Sketch254
  ReferenceAxis = -> Sketch254 [N_Axis]
  Refine = true
  Suppressed = false
  Type = 0
FEATURE [Sketcher::SketchObject] Sketch255
  ArcFitTolerance = 1e-06
  AttachmentSupport = -> [Pad154]
  ExternalGeometry = -> [Pad154]
  FullyConstrained = true
  MakeInternals = false
  MapMode = 5
  Placement = pos=(0,0,3.25) rot=(0,0,1;0rad)
  sketch-geometry (6):
    g0: LineSegment StartX=4.5 StartY=3.4 StartZ=0 EndX=8.85147 EndY=3.4 EndZ=0
    g1: LineSegment StartX=8.85147 StartY=3.4 StartZ=0 EndX=10.9 EndY=1.35147 EndZ=0
    g2: LineSegment StartX=10.9 StartY=1.35147 StartZ=0 EndX=10.9 EndY=-1.35147 EndZ=0
    g3: LineSegment StartX=10.9 StartY=-1.35147 StartZ=0 EndX=8.25147 EndY=-4 EndZ=0
    g4: LineSegment StartX=8.25147 StartY=-4 StartZ=0 EndX=4.5 EndY=-4 EndZ=0
    g5: LineSegment StartX=4.5 StartY=3.4 StartZ=0 EndX=4.5 EndY=-4 EndZ=0
  constraints (17):
    c: PointOnObject(g0,g-8)
    c: Horizontal(g0)
    c: Coincident(g1,g0)
    c: Coincident(g2,g1)
    c: Vertical(g2)
    c: Coincident(g3,g2)
    c: Coincident(g4,g3)
    c: Horizontal(g4)
    c: DistanceX(g1,g-5) = 0.6
    c: DistanceY(g0,g-4) = 0.6
    c: Angle(g0,g1) = 2.35619
    c: Angle(g2,g3) = 2.35619
    c: Distance(g0,g-4) = 0.6
    c: Distance(g3,g-6) = 0.6
    c: Coincident(g5,g0)
    c: Coincident(g5,g4)
    c: Coincident(g4,g-8)
FEATURE [PartDesign::Pad] Pad155
  BaseFeature = -> Pad154
  Direction = (0,0,1)
  Length = 1.7
  Length2 = 10
  Profile = -> Sketch255
  ReferenceAxis = -> Sketch255 [N_Axis]
  Refine = true
  Suppressed = false
  Type = 0
FEATURE [Sketcher::SketchObject] Sketch256
  ArcFitTolerance = 1e-06
  AttachmentSupport = -> [Pad155]
  ExternalGeometry = -> [Pad155]
  FullyConstrained = true
  MakeInternals = false
  MapMode = 5
  Placement = pos=(0,0,1.25) rot=(1,0,0;3.14159rad)
  sketch-geometry (9):
    g0: LineSegment StartX=4.5 StartY=4 StartZ=0 EndX=8.25147 EndY=4 EndZ=0
    g1: LineSegment StartX=8.25147 StartY=4 StartZ=0 EndX=10.7 EndY=1.55147 EndZ=0
    g2: LineSegment StartX=10.7 StartY=1.55147 StartZ=0 EndX=10.7 EndY=-1.55147 EndZ=0
    g3: LineSegment StartX=4.5 StartY=4 StartZ=0 EndX=4.5 EndY=-3.4 EndZ=0
    g4: LineSegment StartX=4.5 StartY=-3.4 StartZ=0 EndX=5.5 EndY=-3.4 EndZ=0
    g5: LineSegment StartX=5.5 StartY=-3.4 StartZ=0 EndX=7 EndY=-1.9 EndZ=0
    g6: LineSegment StartX=10.7 StartY=-1.55147 StartZ=0 EndX=9.45147 EndY=-2.8 EndZ=0
    g7: LineSegment StartX=9.45147 StartY=-2.8 StartZ=0 EndX=7 EndY=-2.8 EndZ=0
    g8: LineSegment StartX=7 StartY=-2.8 StartZ=0 EndX=7 EndY=-1.9 EndZ=0
  constraints (26):
    c: Horizontal(g0)
    c: Coincident(g1,g0)
    c: Coincident(g2,g1)
    c: Vertical(g2)
    c: DistanceX(g2,g-6) = 0.8
    c: Angle(g1,g2) = 2.35619
    c: Coincident(g3,g0)
    c: Vertical(g3)
    c: Coincident(g4,g3)
    c: Horizontal(g4)
    c: Coincident(g5,g4)
    c: Angle(g5,g4) = 2.35619
    c: DistanceY(g-7,g4) = 0.6
    c: DistanceX(g4,g4) = 1
    c: Distance(g2,g-6) = 0.6
    c: Coincident(g0,g-8)
    c: Distance(g1,g-4) = 0.6
    c: Coincident(g6,g2)
    c: Coincident(g7,g6)
    c: Horizontal(g7)
    c: Parallel(g6,g-6)
    c: Coincident(g8,g7)
    c: Vertical(g8)
    c: Coincident(g5,g8)
    c: DistanceX(g-9,g5) = 2.5
    c: DistanceY(g-7,g7) = 1.2
FEATURE [Sketcher::SketchObject] Sketch257
  ArcFitTolerance = 1e-06
  FullyConstrained = true
  MakeInternals = false
  MapMode = 5
  Placement = pos=(0,0,-0.65) rot=(1,0,0;3.14159rad)
  sketch-geometry (8):
    g0: LineSegment StartX=4.5 StartY=4.25 StartZ=0 EndX=7.70147 EndY=4.25 EndZ=0
    g1: LineSegment StartX=7.70147 StartY=4.25 StartZ=0 EndX=10.4 EndY=1.55147 EndZ=0
    g2: LineSegment StartX=10.4 StartY=1.55147 StartZ=0 EndX=10.4 EndY=-1.53431 EndZ=0
    g3: LineSegment StartX=10.4 StartY=-1.53431 StartZ=0 EndX=7.3 EndY=-1.53431 EndZ=0
    g4: LineSegment StartX=7.3 StartY=-1.53431 StartZ=0 EndX=7.3 EndY=-1.55 EndZ=0
    g5: LineSegment StartX=7.3 StartY=-1.55 StartZ=0 EndX=5.5 EndY=-3.35 EndZ=0
    g6: LineSegment StartX=5.5 StartY=-3.35 StartZ=0 EndX=4.5 EndY=-3.35 EndZ=0
    g7: LineSegment StartX=4.5 StartY=-3.35 StartZ=0 EndX=4.5 EndY=4.25 EndZ=0
  constraints (21):
    c: Horizontal(g0)
    c: Coincident(g1,g0)
    c: Coincident(g2,g1)
    c: Vertical(g2)
    c: Coincident(g3,g2)
    c: Horizontal(g3)
    c: Coincident(g4,g3)
    c: Vertical(g4)
    c: Coincident(g5,g4)
    c: Coincident(g6,g5)
    c: Coincident(g7,g6)
    c: Coincident(g7,g0)
    c: Coincident(g0,g-9)
    c: DistanceX(g0,g-4) = 0.3
    c: DistanceX(g1,g-5) = 0.3
    c: Angle(g0,g1) = 2.35619
    c: DistanceY(g-7,g3) = 0.3
    c: Coincident(g6,g-9)
    c: Coincident(g5,g-8)
    c: Angle(g5,g6) = 2.35619
    c: DistanceX(g-8,g3) = 0.3
FEATURE [PartDesign::Pad] Pad156
  BaseFeature = -> Pad155
  Direction = (0,-1e-16,-1)
  Length = 1.9
  Length2 = 10
  Profile = -> Sketch257
  ReferenceAxis = -> Sketch257 [N_Axis]
  Refine = true
  Suppressed = false
  Type = 0
FEATURE [Sketcher::SketchObject] Sketch258
  ArcFitTolerance = 1e-06
  AttachmentSupport = -> [Pad156]
  ExternalGeometry = -> [Pad156]
  FullyConstrained = true
  MakeInternals = false
  MapMode = 5
  Placement = pos=(0,0,4.95) rot=(0,0,1;0rad)
  sketch-geometry (1):
    g0: Circle CenterX=8.075 CenterY=0 CenterZ=0 NormalX=0 NormalY=0 NormalZ=1 AngleXU=0 Radius=1.425
  constraints (3):
    c: Diameter(g0) = 2.85
    c: DistanceX(g-4,g0) = 3.575
    c: PointOnObject(g0,g-1)
FEATURE [PartDesign::Pocket] Pocket104
  BaseFeature = -> Pad156
  Direction = (0,0,-1)
  Length = 6
  Length2 = 5
  Profile = -> Sketch258
  ReferenceAxis = -> Sketch258 [N_Axis]
  Refine = true
  Suppressed = false
  Type = 0
FEATURE [Sketcher::SketchObject] Sketch259
  ArcFitTolerance = 1e-06
  AttachmentSupport = -> [Pocket104]
  ExternalGeometry = -> [Pocket104]
  FullyConstrained = true
  MakeInternals = false
  MapMode = 5
  Placement = pos=(0,4,0) rot=(0,0.707107,0.707107;3.14159rad)
  sketch-geometry (7):
    g0: LineSegment StartX=-4.5 StartY=4.95 StartZ=0 EndX=-8.5 EndY=4.95 EndZ=0
    g1: LineSegment StartX=-8.5 StartY=4.95 StartZ=0 EndX=-9.5 EndY=3.95 EndZ=0
    g2: LineSegment StartX=-9.5 StartY=0.25 StartZ=0 EndX=-7.5 EndY=0.25 EndZ=0
    g3: LineSegment StartX=-7.5 StartY=0.25 StartZ=0 EndX=-7.5 EndY=1.25 EndZ=0
    g4: LineSegment StartX=-7.5 StartY=1.25 StartZ=0 EndX=-4.5 EndY=1.25 EndZ=0
    g5: LineSegment StartX=-4.5 StartY=1.25 StartZ=0 EndX=-4.5 EndY=4.95 EndZ=0
    g6: LineSegment StartX=-9.5 StartY=3.95 StartZ=0 EndX=-9.5 EndY=0.25 EndZ=0
  constraints (19):
    c: Angle(g1,g0) = 2.35619
    c: Coincident(g1,g0)
    c: Coincident(g6,g1)
    c: Vertical(g6)
    c: Coincident(g2,g6)
    c: Horizontal(g0)
    c: Coincident(g0,g5)
    c: Coincident(g0,g-3)
    c: Coincident(g5,g-4)
    c: Coincident(g4,g5)
    c: Horizontal(g2)
    c: Horizontal(g4)
    c: Vertical(g3)
    c: DistanceY(g3,g3) = 1
    c: DistanceX(g0,g0) = 4
    c: DistanceX(g4,g4) = 3
    c: DistanceX(g2,g2) = 2
    c: Coincident(g2,g3)
    c: Coincident(g3,g4)
FEATURE [PartDesign::Pad] Pad157
  BaseFeature = -> Pocket104
  Direction = (0,1,-2e-16)
  Length = 2.5
  Length2 = 10
  Profile = -> Sketch259
  ReferenceAxis = -> Sketch259 [N_Axis]
  Refine = true
  Reversed = true
  Suppressed = false
  Type = 0
FEATURE [PartDesign::Pad] Pad158
  BaseFeature = -> Pad157
  Direction = (0,0,-1)
  Length = 1.9
  Length2 = 10
  Profile = -> Sketch256
  ReferenceAxis = -> Sketch256 [N_Axis]
  Refine = true
  Suppressed = false
  Type = 0
FEATURE [Sketcher::SketchObject] Sketch260
  ArcFitTolerance = 1e-06
  AttachmentSupport = -> [Pad158]
  ExternalGeometry = -> [Pad158]
  FullyConstrained = true
  MakeInternals = false
  MapMode = 5
  Placement = pos=(0,0,-0.65) rot=(1,0,0;3.14159rad)
  sketch-geometry (9):
    g0: LineSegment StartX=4.5 StartY=4 StartZ=0 EndX=4.5 EndY=-3.4 EndZ=0
    g1: LineSegment StartX=4.5 StartY=-3.4 StartZ=0 EndX=5.5 EndY=-3.4 EndZ=0
    g2: LineSegment StartX=5.5 StartY=-3.4 StartZ=0 EndX=7 EndY=-1.9 EndZ=0
    g3: LineSegment StartX=7 StartY=-1.9 StartZ=0 EndX=7 EndY=-2.35 EndZ=0
    g4: LineSegment StartX=7 StartY=-2.35 StartZ=0 EndX=9.23353 EndY=-2.35 EndZ=0
    g5: LineSegment StartX=9.23353 StartY=-2.35 StartZ=0 EndX=10.2178 EndY=-1.41921 EndZ=0
    g6: LineSegment StartX=7.63702 StartY=4 StartZ=0 EndX=10.2178 EndY=1.41921 EndZ=0
    g7: LineSegment StartX=10.2178 StartY=1.41921 StartZ=0 EndX=10.2178 EndY=-1.41921 EndZ=0
    g8: LineSegment StartX=7.63702 StartY=4 StartZ=0 EndX=4.5 EndY=4 EndZ=0
  constraints (22):
    c: Coincident(g0,g-4)
    c: Coincident(g0,g-11)
    c: Coincident(g1,g0)
    c: Coincident(g1,g-11)
    c: Coincident(g2,g1)
    c: Coincident(g2,g-10)
    c: Coincident(g3,g2)
    c: Symmetric(g-9,g-9,g3)
    c: Coincident(g4,g3)
    c: Horizontal(g4)
    c: Coincident(g5,g4)
    c: Coincident(g7,g6)
    c: Coincident(g7,g5)
    c: Vertical(g7)
    c: Angle(g7,g5) = 2.32827
    c: Distance(g6,g-6) = 0.5
    c: Distance(g4,g-8) = 0.5
    c: Distance(g5,g-7) = 0.5
    c: Coincident(g8,g6)
    c: Coincident(g8,g0)
    c: Horizontal(g8)
    c: Angle(g8,g6) = 2.35619
FEATURE [PartDesign::Pad] Pad159
  BaseFeature = -> Pad158
  Direction = (0,0,-1)
  Length = 1.9
  Length2 = 10
  Profile = -> Sketch260
  ReferenceAxis = -> Sketch260 [N_Axis]
  Refine = true
  Suppressed = false
  Type = 0
FEATURE [PartDesign::Fillet] Fillet021
  Base = -> Pad159 [Edge14,Edge8,Edge7,Edge88,Edge76,Edge89]
  BaseFeature = -> Pad159
  Radius = 0.5
  Refine = true
  SupportTransform = false
  Suppressed = false
  UseAllEdges = false
FEATURE [PartDesign::Body] Body008  label="Right_Fist"
  AllowCompound = false
  Group = -> [Sketch250,Pad151,Sketch251,Pad152,Sketch252,Pad153,Sketch253,Pocket103,Sketch254,Pad154,Sketch255,Pad155,Sketch256,Sketch257,Pad156,Sketch258,Pocket104,Sketch259,Pad157,Pad158,Sketch260,Pad159,Fillet021]
  Origin = -> Origin008
  Placement = pos=(4.25,-17.2,4.975) rot=(0,0,1;1.5708rad)
  Tip = -> Fillet021
